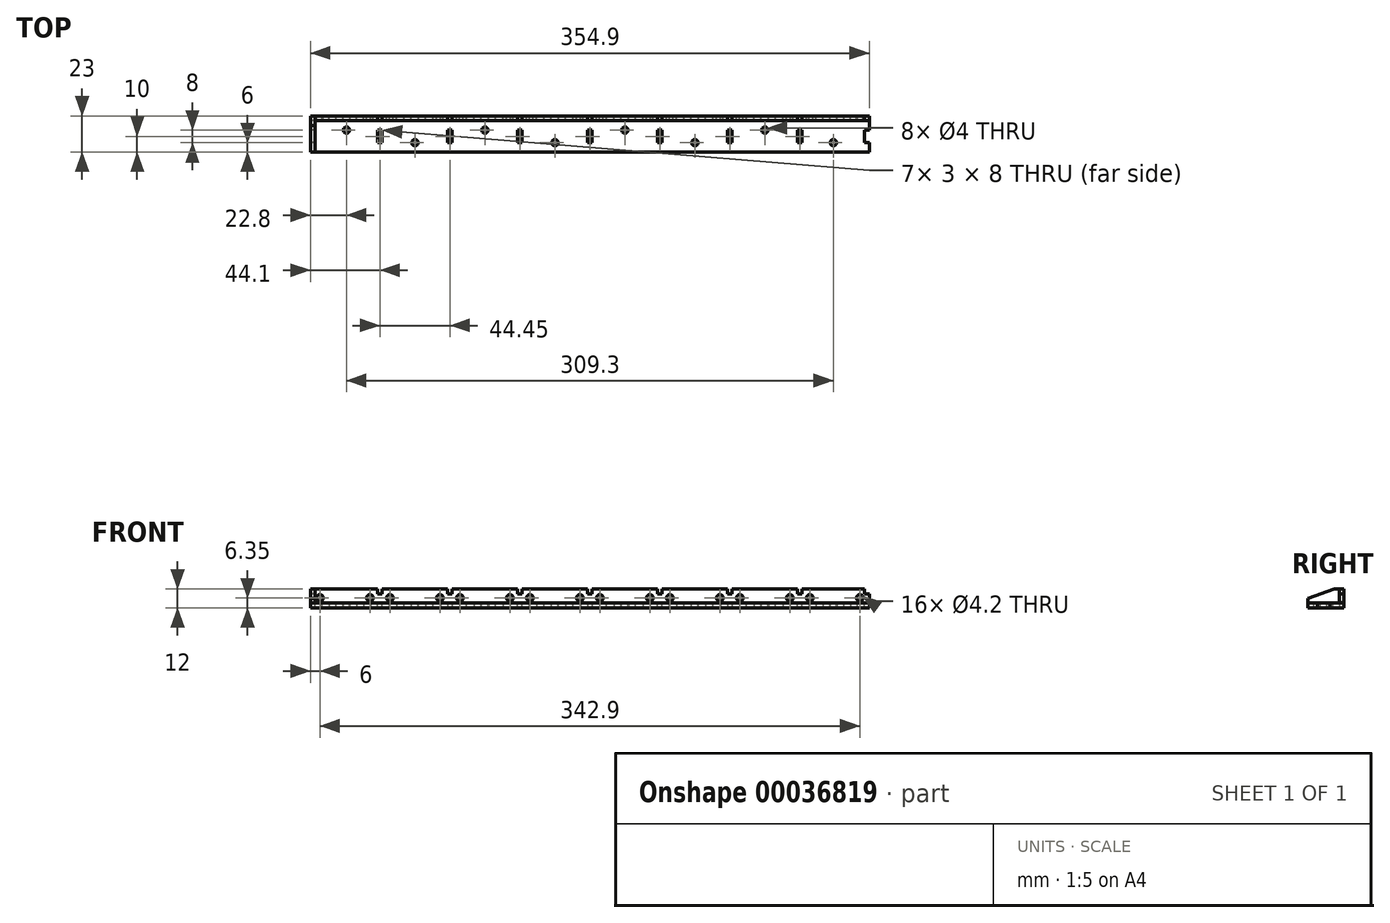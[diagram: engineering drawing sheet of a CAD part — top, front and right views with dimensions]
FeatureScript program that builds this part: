
annotation { "Feature Type Name" : "Feature", "Feature Type Description" : "" }
export const myFeature = defineFeature(function(context is Context, id is Id, definition is map)
    precondition{}
    {
        {
            var Q0;
            Q0=qCreatedBy(makeId("Front.planeOp"),FACE);
            var sketch = newSketch(context, id + "F0", { "sketchPlane" : qUnion([Q0])});
            skLineSegment(sketch, "E0.bottom", {"start": v(0, 0) * mm, "end": v(354.9, 0) * mm});
            skLineSegment(sketch, "E0.top", {"start": v(0, 12) * mm, "end": v(354.9, 12) * mm});
            skLineSegment(sketch, "E0.left", {"start": v(0, 0) * mm, "end": v(0, 12) * mm});
            skLineSegment(sketch, "E0.right", {"start": v(354.9, 0) * mm, "end": v(354.9, 12) * mm});
            skCircle(sketch, "E1", {"center": v(6, 6.35) * mm, "radius": 2.1 * mm});
            skCircle(sketch, "E2", {"center": v(37.75, 6.35) * mm, "radius": 2.1 * mm});
            skCircle(sketch, "E3", {"center": v(50.45, 6.35) * mm, "radius": 2.1 * mm});
            skCircle(sketch, "E4", {"center": v(82.2, 6.35) * mm, "radius": 2.1 * mm});
            skCircle(sketch, "E5", {"center": v(94.9, 6.35) * mm, "radius": 2.1 * mm});
            skCircle(sketch, "E6", {"center": v(126.65, 6.35) * mm, "radius": 2.1 * mm});
            skCircle(sketch, "E7", {"center": v(139.35, 6.35) * mm, "radius": 2.1 * mm});
            skCircle(sketch, "E8", {"center": v(171.1, 6.35) * mm, "radius": 2.1 * mm});
            skCircle(sketch, "E9", {"center": v(183.8, 6.35) * mm, "radius": 2.1 * mm});
            skCircle(sketch, "E10", {"center": v(215.55, 6.35) * mm, "radius": 2.1 * mm});
            skCircle(sketch, "E11", {"center": v(228.25, 6.35) * mm, "radius": 2.1 * mm});
            skCircle(sketch, "E12", {"center": v(260, 6.35) * mm, "radius": 2.1 * mm});
            skCircle(sketch, "E13", {"center": v(272.7, 6.35) * mm, "radius": 2.1 * mm});
            skCircle(sketch, "E14", {"center": v(304.45, 6.35) * mm, "radius": 2.1 * mm});
            skCircle(sketch, "E15", {"center": v(317.15, 6.35) * mm, "radius": 2.1 * mm});
            skCircle(sketch, "E16", {"center": v(348.9, 6.35) * mm, "radius": 2.1 * mm});
            skLineSegment(sketch, "E17", {"start": v(6, 6.35) * mm, "end": v(37.75, 6.35) * mm, "construction": true});
            skLineSegment(sketch, "E18", {"start": v(50.45, 6.35) * mm, "end": v(82.2, 6.35) * mm, "construction": true});
            skLineSegment(sketch, "E19", {"start": v(94.9, 6.35) * mm, "end": v(126.65, 6.35) * mm, "construction": true});
            skLineSegment(sketch, "E20", {"start": v(139.35, 6.35) * mm, "end": v(171.1, 6.35) * mm, "construction": true});
            skLineSegment(sketch, "E21", {"start": v(183.8, 6.35) * mm, "end": v(215.55, 6.35) * mm, "construction": true});
            skLineSegment(sketch, "E22", {"start": v(228.25, 6.35) * mm, "end": v(260, 6.35) * mm, "construction": true});
            skLineSegment(sketch, "E23", {"start": v(272.7, 6.35) * mm, "end": v(304.45, 6.35) * mm, "construction": true});
            skLineSegment(sketch, "E24", {"start": v(317.15, 6.35) * mm, "end": v(348.9, 6.35) * mm, "construction": true});
            skLineSegment(sketch, "E25", {"start": v(37.75, 6.35) * mm, "end": v(50.45, 6.35) * mm, "construction": true});
            skLineSegment(sketch, "E26", {"start": v(82.2, 6.35) * mm, "end": v(94.9, 6.35) * mm, "construction": true});
            skLineSegment(sketch, "E27", {"start": v(126.65, 6.35) * mm, "end": v(139.35, 6.35) * mm, "construction": true});
            skLineSegment(sketch, "E28", {"start": v(171.1, 6.35) * mm, "end": v(183.8, 6.35) * mm, "construction": true});
            skLineSegment(sketch, "E29", {"start": v(215.55, 6.35) * mm, "end": v(228.25, 6.35) * mm, "construction": true});
            skLineSegment(sketch, "E30", {"start": v(260, 6.35) * mm, "end": v(272.7, 6.35) * mm, "construction": true});
            skLineSegment(sketch, "E31", {"start": v(304.45, 6.35) * mm, "end": v(317.15, 6.35) * mm, "construction": true});
            skLineSegment(sketch, "E32", {"start": v(6, 6.35) * mm, "end": v(0, 6.35) * mm, "construction": true});
            skLineSegment(sketch, "E33", {"start": v(348.9, 6.35) * mm, "end": v(354.9, 6.35) * mm, "construction": true});
            skPoint(sketch, "E34", {"position": v(44.1, 6.35) * mm});
            skPoint(sketch, "E35", {"position": v(88.55, 6.35) * mm});
            skPoint(sketch, "E36", {"position": v(133, 6.35) * mm});
            skPoint(sketch, "E37", {"position": v(177.45, 6.35) * mm});
            skPoint(sketch, "E38", {"position": v(221.9, 6.35) * mm});
            skPoint(sketch, "E39", {"position": v(266.35, 6.35) * mm});
            skPoint(sketch, "E40", {"position": v(310.8, 6.35) * mm});
            skCircle(sketch, "E41", {"center": v(50.45, 6.35) * mm, "radius": 2.5 * mm, "construction": true});
            skSolve(sketch);
        }
        {
            var Q0;
            Q0=makeQuery(id+"F0.imprint","IMPRINT",FACE,{"disambiguationData":[TD([[makeQuery(id+"F0.imprint","IMPRINT",EDGE,{"derivedFrom":sQuery(id+"F0.wireOp",EDGE,"E0.bottom")}),1.0]])]});
            var sketch = newSketch(context, id + "F1", { "sketchPlane" : qUnion([Q0])});
            skLineSegment(sketch, "E42", {"start": v(44.1, 6.35) * mm, "end": v(44.1, 0) * mm, "construction": true});
            skLineSegment(sketch, "E43", {"start": v(88.55, 6.35) * mm, "end": v(88.55, 0) * mm, "construction": true});
            skLineSegment(sketch, "E44", {"start": v(133, 6.35) * mm, "end": v(133, 0) * mm, "construction": true});
            skLineSegment(sketch, "E45.MirrorCS", {"start": v(177.45, 6.35) * mm, "end": v(177.45, 0) * mm});
            skLineSegment(sketch, "E46.MirrorCS", {"start": v(221.9, 6.35) * mm, "end": v(221.9, 0) * mm});
            skLineSegment(sketch, "E47", {"start": v(266.35, 6.35) * mm, "end": v(266.35, 0) * mm, "construction": true});
            skLineSegment(sketch, "E48.MirrorCS", {"start": v(310.8, 6.35) * mm, "end": v(310.8, 0) * mm});
            skLineSegment(sketch, "E49.bottom", {"start": v(0, 0) * mm, "end": v(3, 0) * mm});
            skLineSegment(sketch, "E49.top", {"start": v(0, 3) * mm, "end": v(3, 3) * mm});
            skLineSegment(sketch, "E49.left", {"start": v(0, 0) * mm, "end": v(0, 3) * mm});
            skLineSegment(sketch, "E49.right", {"start": v(3, 0) * mm, "end": v(3, 3) * mm});
            skLineSegment(sketch, "E50.bottom", {"start": v(42.6, 0) * mm, "end": v(45.6, 0) * mm});
            skLineSegment(sketch, "E50.top", {"start": v(42.6, 3) * mm, "end": v(45.6, 3) * mm});
            skLineSegment(sketch, "E50.left", {"start": v(42.6, 0) * mm, "end": v(42.6, 3) * mm});
            skLineSegment(sketch, "E50.right", {"start": v(45.6, 0) * mm, "end": v(45.6, 3) * mm});
            skPoint(sketch, "E51", {"position": v(44.1, 0) * mm});
            skLineSegment(sketch, "E52.MirrorCS", {"start": v(354.9, 3) * mm, "end": v(351.9, 3) * mm});
            skLineSegment(sketch, "E53.MirrorCS", {"start": v(351.9, 0) * mm, "end": v(351.9, 3) * mm});
            skLineSegment(sketch, "E54.MirrorCS", {"start": v(354.9, 0) * mm, "end": v(351.9, 0) * mm, "construction": true});
            skLineSegment(sketch, "E55.MirrorCS", {"start": v(354.9, 0) * mm, "end": v(354.9, 3) * mm, "construction": true});
            skLineSegment(sketch, "E56", {"start": v(351.9, 0) * mm, "end": v(354.9, 0) * mm});
            skLineSegment(sketch, "E57", {"start": v(354.9, 3) * mm, "end": v(354.9, 0) * mm});
            skLineSegment(sketch, "E58.MirrorCS", {"start": v(131.5, 0) * mm, "end": v(131.5, 3) * mm});
            skLineSegment(sketch, "E59.MirrorCS", {"start": v(134.5, 0) * mm, "end": v(134.5, 3) * mm});
            skPoint(sketch, "E60.MirrorP", {"position": v(133, 0) * mm});
            skLineSegment(sketch, "E61.MirrorCS", {"start": v(134.5, 3) * mm, "end": v(131.5, 3) * mm});
            skLineSegment(sketch, "E62.MirrorCS", {"start": v(134.5, 0) * mm, "end": v(131.5, 0) * mm});
            skLineSegment(sketch, "E63.MirrorCS", {"start": v(312.3, 0) * mm, "end": v(309.3, 0) * mm});
            skLineSegment(sketch, "E64.MirrorCS", {"start": v(312.3, 0) * mm, "end": v(312.3, 3) * mm});
            skLineSegment(sketch, "E65.MirrorCS", {"start": v(309.3, 0) * mm, "end": v(309.3, 3) * mm});
            skLineSegment(sketch, "E66.MirrorCS", {"start": v(312.3, 3) * mm, "end": v(309.3, 3) * mm});
            skPoint(sketch, "E67.MirrorP", {"position": v(310.8, 0) * mm});
            skLineSegment(sketch, "E68.MirrorCS", {"start": v(220.4, 0) * mm, "end": v(223.4, 0) * mm});
            skLineSegment(sketch, "E69.MirrorCS", {"start": v(223.4, 0) * mm, "end": v(223.4, 3) * mm});
            skLineSegment(sketch, "E70.MirrorCS", {"start": v(220.4, 0) * mm, "end": v(220.4, 3) * mm});
            skLineSegment(sketch, "E71.MirrorCS", {"start": v(220.4, 3) * mm, "end": v(223.4, 3) * mm});
            skLineSegment(sketch, "E72.bottom", {"start": v(87.05, 3) * mm, "end": v(90.05, 3) * mm});
            skLineSegment(sketch, "E72.top", {"start": v(87.05, 0) * mm, "end": v(90.05, 0) * mm});
            skLineSegment(sketch, "E72.left", {"start": v(87.05, 3) * mm, "end": v(87.05, 0) * mm});
            skLineSegment(sketch, "E72.right", {"start": v(90.05, 3) * mm, "end": v(90.05, 0) * mm});
            skLineSegment(sketch, "E73.MirrorCS", {"start": v(178.95, 3) * mm, "end": v(175.95, 3) * mm});
            skLineSegment(sketch, "E74.MirrorCS", {"start": v(178.95, 3) * mm, "end": v(178.95, 0) * mm});
            skLineSegment(sketch, "E75.MirrorCS", {"start": v(178.95, 0) * mm, "end": v(175.95, 0) * mm});
            skLineSegment(sketch, "E76.MirrorCS", {"start": v(175.95, 3) * mm, "end": v(175.95, 0) * mm});
            skLineSegment(sketch, "E77.MirrorCS", {"start": v(264.85, 3) * mm, "end": v(267.85, 3) * mm});
            skLineSegment(sketch, "E78.MirrorCS", {"start": v(264.85, 0) * mm, "end": v(267.85, 0) * mm});
            skLineSegment(sketch, "E79.MirrorCS", {"start": v(267.85, 3) * mm, "end": v(267.85, 0) * mm});
            skLineSegment(sketch, "E80.MirrorCS", {"start": v(264.85, 3) * mm, "end": v(264.85, 0) * mm});
            skLineSegment(sketch, "E81", {"start": v(42.6, 3) * mm, "end": v(38.2, 3) * mm, "construction": true});
            skLineSegment(sketch, "E82", {"start": v(38.2, 3) * mm, "end": v(33.8, 3) * mm});
            skLineSegment(sketch, "E83", {"start": v(33.8, 3) * mm, "end": v(29.4, 3) * mm, "construction": true});
            skLineSegment(sketch, "E84", {"start": v(29.4, 3) * mm, "end": v(25, 3) * mm});
            skLineSegment(sketch, "E85", {"start": v(25, 3) * mm, "end": v(20.6, 3) * mm, "construction": true});
            skLineSegment(sketch, "E86", {"start": v(20.6, 3) * mm, "end": v(16.2, 3) * mm});
            skLineSegment(sketch, "E87", {"start": v(16.2, 3) * mm, "end": v(11.8, 3) * mm, "construction": true});
            skLineSegment(sketch, "E88", {"start": v(11.8, 3) * mm, "end": v(7.4, 3) * mm});
            skLineSegment(sketch, "E89", {"start": v(7.4, 3) * mm, "end": v(3, 3) * mm, "construction": true});
            skLineSegment(sketch, "E90", {"start": v(38.2, 3) * mm, "end": v(38.2, 0) * mm});
            skLineSegment(sketch, "E91", {"start": v(33.8, 3) * mm, "end": v(33.8, 0) * mm});
            skLineSegment(sketch, "E92", {"start": v(33.8, 0) * mm, "end": v(38.2, 0) * mm});
            skLineSegment(sketch, "E93", {"start": v(29.4, 3) * mm, "end": v(29.4, 0) * mm});
            skLineSegment(sketch, "E94", {"start": v(29.4, 0) * mm, "end": v(25, 0) * mm});
            skLineSegment(sketch, "E95", {"start": v(25, 0) * mm, "end": v(25, 3) * mm});
            skLineSegment(sketch, "E96", {"start": v(20.6, 3) * mm, "end": v(20.6, 0) * mm});
            skLineSegment(sketch, "E97", {"start": v(20.6, 0) * mm, "end": v(16.2, 0) * mm});
            skLineSegment(sketch, "E98", {"start": v(16.2, 0) * mm, "end": v(16.2, 3) * mm});
            skLineSegment(sketch, "E99", {"start": v(11.8, 3) * mm, "end": v(11.8, 0) * mm});
            skLineSegment(sketch, "E100", {"start": v(11.8, 0) * mm, "end": v(7.4, 0) * mm});
            skLineSegment(sketch, "E101", {"start": v(7.4, 0) * mm, "end": v(7.4, 3) * mm});
            skLineSegment(sketch, "E102.MirrorCS", {"start": v(325.5, 3) * mm, "end": v(329.9, 3) * mm});
            skLineSegment(sketch, "E103.MirrorCS", {"start": v(329.9, 0) * mm, "end": v(329.9, 3) * mm});
            skLineSegment(sketch, "E104.MirrorCS", {"start": v(325.5, 0) * mm, "end": v(329.9, 0) * mm});
            skLineSegment(sketch, "E105.MirrorCS", {"start": v(321.1, 3) * mm, "end": v(325.5, 3) * mm, "construction": true});
            skLineSegment(sketch, "E106.MirrorCS", {"start": v(338.7, 3) * mm, "end": v(343.1, 3) * mm, "construction": true});
            skLineSegment(sketch, "E107.MirrorCS", {"start": v(329.9, 3) * mm, "end": v(334.3, 3) * mm, "construction": true});
            skLineSegment(sketch, "E108.MirrorCS", {"start": v(334.3, 0) * mm, "end": v(338.7, 0) * mm});
            skLineSegment(sketch, "E109.MirrorCS", {"start": v(334.3, 3) * mm, "end": v(338.7, 3) * mm});
            skLineSegment(sketch, "E110.MirrorCS", {"start": v(316.7, 3) * mm, "end": v(316.7, 0) * mm});
            skLineSegment(sketch, "E111.MirrorCS", {"start": v(316.7, 3) * mm, "end": v(321.1, 3) * mm});
            skLineSegment(sketch, "E112.MirrorCS", {"start": v(334.3, 3) * mm, "end": v(334.3, 0) * mm});
            skLineSegment(sketch, "E113.MirrorCS", {"start": v(321.1, 3) * mm, "end": v(321.1, 0) * mm});
            skLineSegment(sketch, "E114.MirrorCS", {"start": v(338.7, 0) * mm, "end": v(338.7, 3) * mm});
            skLineSegment(sketch, "E115.MirrorCS", {"start": v(325.5, 3) * mm, "end": v(325.5, 0) * mm});
            skLineSegment(sketch, "E116.MirrorCS", {"start": v(343.1, 3) * mm, "end": v(343.1, 0) * mm});
            skLineSegment(sketch, "E117.MirrorCS", {"start": v(347.5, 0) * mm, "end": v(347.5, 3) * mm});
            skLineSegment(sketch, "E118.MirrorCS", {"start": v(343.1, 0) * mm, "end": v(347.5, 0) * mm});
            skLineSegment(sketch, "E119.MirrorCS", {"start": v(321.1, 0) * mm, "end": v(316.7, 0) * mm});
            skLineSegment(sketch, "E120.MirrorCS", {"start": v(343.1, 3) * mm, "end": v(347.5, 3) * mm});
            skLineSegment(sketch, "E121", {"start": v(59.42, 3) * mm, "end": v(64.02, 3) * mm});
            skLineSegment(sketch, "E122", {"start": v(64.02, 3) * mm, "end": v(68.63, 3) * mm, "construction": true});
            skLineSegment(sketch, "E123", {"start": v(68.63, 3) * mm, "end": v(73.23, 3) * mm});
            skLineSegment(sketch, "E124", {"start": v(73.23, 3) * mm, "end": v(77.84, 3) * mm, "construction": true});
            skLineSegment(sketch, "E125", {"start": v(77.84, 3) * mm, "end": v(82.44, 3) * mm});
            skLineSegment(sketch, "E126", {"start": v(82.44, 3) * mm, "end": v(87.05, 3) * mm, "construction": true});
            skLineSegment(sketch, "E127", {"start": v(82.44, 3) * mm, "end": v(82.44, 0) * mm});
            skLineSegment(sketch, "E128", {"start": v(82.44, 0) * mm, "end": v(77.84, 0) * mm});
            skLineSegment(sketch, "E129", {"start": v(77.84, 0) * mm, "end": v(77.84, 3) * mm});
            skLineSegment(sketch, "E130", {"start": v(73.23, 3) * mm, "end": v(73.23, 0) * mm});
            skLineSegment(sketch, "E131", {"start": v(73.23, 0) * mm, "end": v(68.63, 0) * mm});
            skLineSegment(sketch, "E132", {"start": v(68.63, 0) * mm, "end": v(68.63, 3) * mm});
            skLineSegment(sketch, "E133", {"start": v(64.02, 3) * mm, "end": v(64.02, 0) * mm});
            skLineSegment(sketch, "E134", {"start": v(64.02, 0) * mm, "end": v(59.42, 0) * mm});
            skLineSegment(sketch, "E135", {"start": v(59.42, 0) * mm, "end": v(59.42, 3) * mm});
            skLineSegment(sketch, "E136", {"start": v(59.42, 3) * mm, "end": v(54.81, 3) * mm, "construction": true});
            skLineSegment(sketch, "E137", {"start": v(54.81, 3) * mm, "end": v(54.81, 0) * mm});
            skLineSegment(sketch, "E138", {"start": v(54.81, 0) * mm, "end": v(50.2, 0) * mm});
            skLineSegment(sketch, "E139", {"start": v(50.2, 0) * mm, "end": v(50.2, 3) * mm});
            skLineSegment(sketch, "E140", {"start": v(50.2, 3) * mm, "end": v(54.81, 3) * mm});
            skLineSegment(sketch, "E141", {"start": v(50.2, 3) * mm, "end": v(45.6, 3) * mm, "construction": true});
            skLineSegment(sketch, "E142.MirrorCS", {"start": v(113.08, 3) * mm, "end": v(113.08, 0) * mm});
            skLineSegment(sketch, "E143.MirrorCS", {"start": v(122.29, 3) * mm, "end": v(122.29, 0) * mm});
            skLineSegment(sketch, "E144.MirrorCS", {"start": v(126.9, 0) * mm, "end": v(126.9, 3) * mm});
            skLineSegment(sketch, "E145.MirrorCS", {"start": v(94.66, 3) * mm, "end": v(94.66, 0) * mm});
            skLineSegment(sketch, "E146.MirrorCS", {"start": v(117.68, 3) * mm, "end": v(122.29, 3) * mm, "construction": true});
            skLineSegment(sketch, "E147.MirrorCS", {"start": v(113.08, 0) * mm, "end": v(117.68, 0) * mm});
            skLineSegment(sketch, "E148.MirrorCS", {"start": v(113.08, 3) * mm, "end": v(108.47, 3) * mm, "construction": true});
            skLineSegment(sketch, "E149.MirrorCS", {"start": v(103.87, 3) * mm, "end": v(99.26, 3) * mm, "construction": true});
            skLineSegment(sketch, "E150.MirrorCS", {"start": v(103.87, 0) * mm, "end": v(108.47, 0) * mm});
            skLineSegment(sketch, "E151.MirrorCS", {"start": v(117.68, 3) * mm, "end": v(113.08, 3) * mm});
            skLineSegment(sketch, "E152.MirrorCS", {"start": v(117.68, 0) * mm, "end": v(117.68, 3) * mm});
            skLineSegment(sketch, "E153.MirrorCS", {"start": v(108.47, 3) * mm, "end": v(103.87, 3) * mm});
            skLineSegment(sketch, "E154.MirrorCS", {"start": v(99.26, 3) * mm, "end": v(94.66, 3) * mm});
            skLineSegment(sketch, "E155.MirrorCS", {"start": v(103.87, 3) * mm, "end": v(103.87, 0) * mm});
            skLineSegment(sketch, "E156.MirrorCS", {"start": v(108.47, 0) * mm, "end": v(108.47, 3) * mm});
            skLineSegment(sketch, "E157.MirrorCS", {"start": v(99.26, 0) * mm, "end": v(99.26, 3) * mm});
            skLineSegment(sketch, "E158.MirrorCS", {"start": v(122.29, 0) * mm, "end": v(126.9, 0) * mm});
            skLineSegment(sketch, "E159.MirrorCS", {"start": v(94.66, 0) * mm, "end": v(99.26, 0) * mm});
            skLineSegment(sketch, "E160.MirrorCS", {"start": v(126.9, 3) * mm, "end": v(122.29, 3) * mm});
            skLineSegment(sketch, "E161.MirrorCS", {"start": v(148.32, 3) * mm, "end": v(143.71, 3) * mm, "construction": true});
            skLineSegment(sketch, "E162.MirrorCS", {"start": v(148.32, 3) * mm, "end": v(152.92, 3) * mm});
            skLineSegment(sketch, "E163.MirrorCS", {"start": v(157.53, 3) * mm, "end": v(162.13, 3) * mm});
            skLineSegment(sketch, "E164.MirrorCS", {"start": v(162.13, 3) * mm, "end": v(166.74, 3) * mm, "construction": true});
            skLineSegment(sketch, "E165.MirrorCS", {"start": v(152.92, 3) * mm, "end": v(157.53, 3) * mm, "construction": true});
            skLineSegment(sketch, "E166.MirrorCS", {"start": v(143.71, 3) * mm, "end": v(143.71, 0) * mm});
            skLineSegment(sketch, "E167.MirrorCS", {"start": v(162.13, 3) * mm, "end": v(162.13, 0) * mm});
            skLineSegment(sketch, "E168.MirrorCS", {"start": v(171.34, 0) * mm, "end": v(166.74, 0) * mm});
            skLineSegment(sketch, "E169.MirrorCS", {"start": v(139.1, 0) * mm, "end": v(139.1, 3) * mm});
            skLineSegment(sketch, "E170.MirrorCS", {"start": v(171.34, 3) * mm, "end": v(171.34, 0) * mm});
            skLineSegment(sketch, "E171.MirrorCS", {"start": v(148.32, 0) * mm, "end": v(148.32, 3) * mm});
            skLineSegment(sketch, "E172.MirrorCS", {"start": v(157.53, 0) * mm, "end": v(157.53, 3) * mm});
            skLineSegment(sketch, "E173.MirrorCS", {"start": v(166.74, 3) * mm, "end": v(171.34, 3) * mm});
            skLineSegment(sketch, "E174.MirrorCS", {"start": v(152.92, 0) * mm, "end": v(148.32, 0) * mm});
            skLineSegment(sketch, "E175.MirrorCS", {"start": v(152.92, 3) * mm, "end": v(152.92, 0) * mm});
            skLineSegment(sketch, "E176.MirrorCS", {"start": v(162.13, 0) * mm, "end": v(157.53, 0) * mm});
            skLineSegment(sketch, "E177.MirrorCS", {"start": v(166.74, 0) * mm, "end": v(166.74, 3) * mm});
            skLineSegment(sketch, "E178.MirrorCS", {"start": v(143.71, 0) * mm, "end": v(139.1, 0) * mm});
            skLineSegment(sketch, "E179.MirrorCS", {"start": v(139.1, 3) * mm, "end": v(143.71, 3) * mm});
            skLineSegment(sketch, "E180.MirrorCS", {"start": v(206.58, 3) * mm, "end": v(211.19, 3) * mm, "construction": true});
            skLineSegment(sketch, "E181.MirrorCS", {"start": v(192.77, 3) * mm, "end": v(188.16, 3) * mm, "construction": true});
            skLineSegment(sketch, "E182.MirrorCS", {"start": v(201.98, 3) * mm, "end": v(197.37, 3) * mm, "construction": true});
            skLineSegment(sketch, "E183.MirrorCS", {"start": v(197.37, 3) * mm, "end": v(192.77, 3) * mm});
            skLineSegment(sketch, "E184.MirrorCS", {"start": v(206.58, 3) * mm, "end": v(201.98, 3) * mm});
            skLineSegment(sketch, "E185.MirrorCS", {"start": v(183.56, 3) * mm, "end": v(183.56, 0) * mm});
            skLineSegment(sketch, "E186.MirrorCS", {"start": v(211.19, 3) * mm, "end": v(211.19, 0) * mm});
            skLineSegment(sketch, "E187.MirrorCS", {"start": v(197.37, 0) * mm, "end": v(197.37, 3) * mm});
            skLineSegment(sketch, "E188.MirrorCS", {"start": v(201.98, 3) * mm, "end": v(201.98, 0) * mm});
            skLineSegment(sketch, "E189.MirrorCS", {"start": v(188.16, 3) * mm, "end": v(183.56, 3) * mm});
            skLineSegment(sketch, "E190.MirrorCS", {"start": v(215.8, 0) * mm, "end": v(215.8, 3) * mm});
            skLineSegment(sketch, "E191.MirrorCS", {"start": v(192.77, 3) * mm, "end": v(192.77, 0) * mm});
            skLineSegment(sketch, "E192.MirrorCS", {"start": v(192.77, 0) * mm, "end": v(197.37, 0) * mm});
            skLineSegment(sketch, "E193.MirrorCS", {"start": v(183.56, 0) * mm, "end": v(188.16, 0) * mm});
            skLineSegment(sketch, "E194.MirrorCS", {"start": v(206.58, 0) * mm, "end": v(206.58, 3) * mm});
            skLineSegment(sketch, "E195.MirrorCS", {"start": v(188.16, 0) * mm, "end": v(188.16, 3) * mm});
            skLineSegment(sketch, "E196.MirrorCS", {"start": v(201.98, 0) * mm, "end": v(206.58, 0) * mm});
            skLineSegment(sketch, "E197.MirrorCS", {"start": v(215.8, 3) * mm, "end": v(211.19, 3) * mm});
            skLineSegment(sketch, "E198.MirrorCS", {"start": v(211.19, 0) * mm, "end": v(215.8, 0) * mm});
            skLineSegment(sketch, "E199.MirrorCS", {"start": v(251.03, 3) * mm, "end": v(255.64, 3) * mm, "construction": true});
            skLineSegment(sketch, "E200.MirrorCS", {"start": v(241.82, 3) * mm, "end": v(246.43, 3) * mm, "construction": true});
            skLineSegment(sketch, "E201.MirrorCS", {"start": v(237.22, 3) * mm, "end": v(232.61, 3) * mm, "construction": true});
            skLineSegment(sketch, "E202.MirrorCS", {"start": v(237.22, 3) * mm, "end": v(241.82, 3) * mm});
            skLineSegment(sketch, "E203.MirrorCS", {"start": v(260.24, 0) * mm, "end": v(255.64, 0) * mm});
            skLineSegment(sketch, "E204.MirrorCS", {"start": v(241.82, 0) * mm, "end": v(237.22, 0) * mm});
            skLineSegment(sketch, "E205.MirrorCS", {"start": v(228, 0) * mm, "end": v(228, 3) * mm});
            skLineSegment(sketch, "E206.MirrorCS", {"start": v(241.82, 3) * mm, "end": v(241.82, 0) * mm});
            skLineSegment(sketch, "E207.MirrorCS", {"start": v(260.24, 3) * mm, "end": v(260.24, 0) * mm});
            skLineSegment(sketch, "E208.MirrorCS", {"start": v(232.61, 0) * mm, "end": v(228, 0) * mm});
            skLineSegment(sketch, "E209.MirrorCS", {"start": v(251.03, 3) * mm, "end": v(251.03, 0) * mm});
            skLineSegment(sketch, "E210.MirrorCS", {"start": v(246.43, 0) * mm, "end": v(246.43, 3) * mm});
            skLineSegment(sketch, "E211.MirrorCS", {"start": v(228, 3) * mm, "end": v(232.61, 3) * mm});
            skLineSegment(sketch, "E212.MirrorCS", {"start": v(232.61, 3) * mm, "end": v(232.61, 0) * mm});
            skLineSegment(sketch, "E213.MirrorCS", {"start": v(255.64, 3) * mm, "end": v(260.24, 3) * mm});
            skLineSegment(sketch, "E214.MirrorCS", {"start": v(255.64, 0) * mm, "end": v(255.64, 3) * mm});
            skLineSegment(sketch, "E215.MirrorCS", {"start": v(237.22, 0) * mm, "end": v(237.22, 3) * mm});
            skLineSegment(sketch, "E216.MirrorCS", {"start": v(246.43, 3) * mm, "end": v(251.03, 3) * mm});
            skLineSegment(sketch, "E217.MirrorCS", {"start": v(251.03, 0) * mm, "end": v(246.43, 0) * mm});
            skLineSegment(sketch, "E218.MirrorCS", {"start": v(295.48, 3) * mm, "end": v(290.88, 3) * mm});
            skLineSegment(sketch, "E219.MirrorCS", {"start": v(286.27, 3) * mm, "end": v(281.67, 3) * mm});
            skLineSegment(sketch, "E220.MirrorCS", {"start": v(295.48, 3) * mm, "end": v(300.09, 3) * mm, "construction": true});
            skLineSegment(sketch, "E221.MirrorCS", {"start": v(290.88, 3) * mm, "end": v(286.27, 3) * mm, "construction": true});
            skLineSegment(sketch, "E222.MirrorCS", {"start": v(281.67, 3) * mm, "end": v(277.06, 3) * mm, "construction": true});
            skLineSegment(sketch, "E223.MirrorCS", {"start": v(272.46, 3) * mm, "end": v(272.46, 0) * mm});
            skLineSegment(sketch, "E224.MirrorCS", {"start": v(281.67, 3) * mm, "end": v(281.67, 0) * mm});
            skLineSegment(sketch, "E225.MirrorCS", {"start": v(286.27, 0) * mm, "end": v(286.27, 3) * mm});
            skLineSegment(sketch, "E226.MirrorCS", {"start": v(304.7, 3) * mm, "end": v(300.09, 3) * mm});
            skLineSegment(sketch, "E227.MirrorCS", {"start": v(290.88, 3) * mm, "end": v(290.88, 0) * mm});
            skLineSegment(sketch, "E228.MirrorCS", {"start": v(295.48, 0) * mm, "end": v(295.48, 3) * mm});
            skLineSegment(sketch, "E229.MirrorCS", {"start": v(304.7, 0) * mm, "end": v(304.7, 3) * mm});
            skLineSegment(sketch, "E230.MirrorCS", {"start": v(290.88, 0) * mm, "end": v(295.48, 0) * mm});
            skLineSegment(sketch, "E231.MirrorCS", {"start": v(272.46, 0) * mm, "end": v(277.06, 0) * mm});
            skLineSegment(sketch, "E232.MirrorCS", {"start": v(277.06, 3) * mm, "end": v(272.46, 3) * mm});
            skLineSegment(sketch, "E233.MirrorCS", {"start": v(300.09, 0) * mm, "end": v(304.7, 0) * mm});
            skLineSegment(sketch, "E234.MirrorCS", {"start": v(300.09, 3) * mm, "end": v(300.09, 0) * mm});
            skLineSegment(sketch, "E235.MirrorCS", {"start": v(281.67, 0) * mm, "end": v(286.27, 0) * mm});
            skLineSegment(sketch, "E236.MirrorCS", {"start": v(277.06, 0) * mm, "end": v(277.06, 3) * mm});
            skSolve(sketch);
        }
        {
            var Q0;
            Q0=qCreatedBy(makeId("Front.planeOp"),FACE);
            var sketch = newSketch(context, id + "F2", { "sketchPlane" : qUnion([Q0])});
            skLineSegment(sketch, "E237.bottom", {"start": v(0, 0) * mm, "end": v(354.9, 0) * mm});
            skLineSegment(sketch, "E237.top", {"start": v(0, 3) * mm, "end": v(354.9, 3) * mm});
            skLineSegment(sketch, "E237.left", {"start": v(0, 0) * mm, "end": v(0, 3) * mm});
            skLineSegment(sketch, "E237.right", {"start": v(354.9, 0) * mm, "end": v(354.9, 3) * mm});
            skSolve(sketch);
        }
        {
            var Q0;
            Q0 = qSketchRegion(id + "F0", true);
            extrude(context, id + "F3", {"entities" : qUnion([Q0]), "offsetDistance" : 25 * mm, "depth" : 3 * mm});
        }
        {
            var Q0;
            Q0=makeQuery(id+"F1.imprint","IMPRINT",FACE,{"disambiguationData":[TD([[makeQuery(id+"F1.imprint","IMPRINT",EDGE,{"derivedFrom":sQuery(id+"F1.wireOp",EDGE,"E49.bottom")}),1.0]])]});
            var Q1;
            Q1=makeQuery(id+"F1.imprint","IMPRINT",FACE,{"disambiguationData":[TD([[makeQuery(id+"F1.imprint","IMPRINT",EDGE,{"derivedFrom":sQuery(id+"F1.wireOp",EDGE,"6a9f6b4e-8c17-479e-95aa-c868ed02bcc8.bottom")}),1.0]])]});
            var Q2;
            Q2=makeQuery(id+"F1.imprint","IMPRINT",FACE,{"disambiguationData":[TD([[makeQuery(id+"F1.imprint","IMPRINT",EDGE,{"derivedFrom":sQuery(id+"F1.wireOp",EDGE,"d0e4a734-2a00-432a-b971-5d8aa04fd6d9.bottom")}),1.0]])]});
            var Q3;
            Q3=makeQuery(id+"F1.imprint","IMPRINT",FACE,{"disambiguationData":[TD([[makeQuery(id+"F1.imprint","IMPRINT",EDGE,{"derivedFrom":sQuery(id+"F1.wireOp",EDGE,"0fa12c67-d307-4137-8aa7-c6dfb889ed58.bottom")}),1.0]])]});
            var Q4;
            Q4=makeQuery(id+"F1.imprint","IMPRINT",FACE,{"disambiguationData":[TD([[makeQuery(id+"F1.imprint","IMPRINT",EDGE,{"derivedFrom":sQuery(id+"F1.wireOp",EDGE,"b24369ca-d6b9-488d-87b8-04e79b56e681.bottom")}),1.0]])]});
            var Q5;
            Q5=makeQuery(id+"F1.imprint","IMPRINT",FACE,{"disambiguationData":[TD([[makeQuery(id+"F1.imprint","IMPRINT",EDGE,{"derivedFrom":sQuery(id+"F1.wireOp",EDGE,"bdd40437-d99c-4cb8-ad16-0bfbec51b95a.bottom")}),1.0]])]});
            var Q6;
            Q6=makeQuery(id+"F1.imprint","IMPRINT",FACE,{"disambiguationData":[TD([[makeQuery(id+"F1.imprint","IMPRINT",EDGE,{"derivedFrom":sQuery(id+"F1.wireOp",EDGE,"855304bd-eab8-4061-b494-b8053609a213.bottom")}),1.0]])]});
            var Q7;
            Q7=makeQuery(id+"F1.imprint","IMPRINT",FACE,{"disambiguationData":[TD([[makeQuery(id+"F1.imprint","IMPRINT",EDGE,{"derivedFrom":sQuery(id+"F1.wireOp",EDGE,"E50.bottom")}),1.0]])]});
            var Q8;
            Q8=makeQuery(id+"F1.imprint","IMPRINT",FACE,{"disambiguationData":[TD([[makeQuery(id+"F1.imprint","IMPRINT",EDGE,{"derivedFrom":sQuery(id+"F1.wireOp",EDGE,"8a604169-f9db-4d10-b6de-17cdce77b9ee2.MirrorCS")}),-1.0]])]});
            var Q9;
            Q9=makeQuery(id+"F1.imprint","IMPRINT",FACE,{"disambiguationData":[TD([[makeQuery(id+"F1.imprint","IMPRINT",EDGE,{"derivedFrom":sQuery(id+"F1.wireOp",EDGE,"8a604169-f9db-4d10-b6de-17cdce77b9ee7.MirrorCS")}),1.0]])]});
            var Q10;
            Q10=makeQuery(id+"F1.imprint","IMPRINT",FACE,{"disambiguationData":[TD([[makeQuery(id+"F1.imprint","IMPRINT",EDGE,{"derivedFrom":sQuery(id+"F1.wireOp",EDGE,"8a604169-f9db-4d10-b6de-17cdce77b9ee4.MirrorCS")}),-1.0]])]});
            var Q11;
            Q11=makeQuery(id+"F1.imprint","IMPRINT",FACE,{"disambiguationData":[TD([[makeQuery(id+"F1.imprint","IMPRINT",EDGE,{"derivedFrom":sQuery(id+"F1.wireOp",EDGE,"8a604169-f9db-4d10-b6de-17cdce77b9ee6.MirrorCS")}),1.0]])]});
            var Q12;
            Q12=makeQuery(id+"F1.imprint","IMPRINT",FACE,{"disambiguationData":[TD([[makeQuery(id+"F1.imprint","IMPRINT",EDGE,{"derivedFrom":sQuery(id+"F1.wireOp",EDGE,"8a604169-f9db-4d10-b6de-17cdce77b9ee1.MirrorCS")}),1.0]])]});
            var Q13;
            Q13=makeQuery(id+"F1.imprint","IMPRINT",FACE,{"disambiguationData":[TD([[makeQuery(id+"F1.imprint","IMPRINT",EDGE,{"derivedFrom":sQuery(id+"F1.wireOp",EDGE,"8a604169-f9db-4d10-b6de-17cdce77b9ee11.MirrorCS")}),1.0]])]});
            var Q14;
            Q14=makeQuery(id+"F1.imprint","IMPRINT",FACE,{"disambiguationData":[TD([[makeQuery(id+"F1.imprint","IMPRINT",EDGE,{"derivedFrom":sQuery(id+"F1.wireOp",EDGE,"2bd68e58-e41e-494a-8911-974b16a43e85.bottom")}),1.0]])]});
            var Q15;
            Q15=makeQuery(id+"F1.imprint","IMPRINT",FACE,{"disambiguationData":[TD([[makeQuery(id+"F1.imprint","IMPRINT",EDGE,{"derivedFrom":sQuery(id+"F1.wireOp",EDGE,"ef449be0-296d-467a-9b3b-92f5416e835a13.MirrorCS")}),1.0]])]});
            var Q16;
            Q16=makeQuery(id+"F1.imprint","IMPRINT",FACE,{"disambiguationData":[TD([[makeQuery(id+"F1.imprint","IMPRINT",EDGE,{"derivedFrom":sQuery(id+"F1.wireOp",EDGE,"ef449be0-296d-467a-9b3b-92f5416e835a5.MirrorCS")}),-1.0]])]});
            var Q17;
            Q17=makeQuery(id+"F1.imprint","IMPRINT",FACE,{"disambiguationData":[TD([[makeQuery(id+"F1.imprint","IMPRINT",EDGE,{"derivedFrom":sQuery(id+"F1.wireOp",EDGE,"ef449be0-296d-467a-9b3b-92f5416e835a1.MirrorCS")}),-1.0]])]});
            var Q18;
            Q18=makeQuery(id+"F1.imprint","IMPRINT",FACE,{"disambiguationData":[TD([[makeQuery(id+"F1.imprint","IMPRINT",EDGE,{"derivedFrom":sQuery(id+"F1.wireOp",EDGE,"ef449be0-296d-467a-9b3b-92f5416e835a6.MirrorCS")}),-1.0]])]});
            var Q19;
            Q19=makeQuery(id+"F1.imprint","IMPRINT",FACE,{"disambiguationData":[TD([[makeQuery(id+"F1.imprint","IMPRINT",EDGE,{"derivedFrom":sQuery(id+"F1.wireOp",EDGE,"ef449be0-296d-467a-9b3b-92f5416e835a8.MirrorCS")}),-1.0]])]});
            var Q20;
            Q20=makeQuery(id+"F1.imprint","IMPRINT",FACE,{"disambiguationData":[TD([[makeQuery(id+"F1.imprint","IMPRINT",EDGE,{"derivedFrom":sQuery(id+"F1.wireOp",EDGE,"ef449be0-296d-467a-9b3b-92f5416e835a15.MirrorCS")}),-1.0]])]});
            var Q21;
            Q21=makeQuery(id+"F1.imprint","IMPRINT",FACE,{"disambiguationData":[TD([[makeQuery(id+"F1.imprint","IMPRINT",EDGE,{"derivedFrom":sQuery(id+"F1.wireOp",EDGE,"d6889f29-3aff-4a43-887b-f05846102f70.bottom")}),1.0]])]});
            var Q22;
            Q22=makeQuery(id+"F1.imprint","IMPRINT",FACE,{"disambiguationData":[TD([[makeQuery(id+"F1.imprint","IMPRINT",EDGE,{"derivedFrom":sQuery(id+"F1.wireOp",EDGE,"3edb70b5-b804-4be9-ab85-b3a438d2129227.MirrorCS")}),1.0]])]});
            var Q23;
            Q23=makeQuery(id+"F1.imprint","IMPRINT",FACE,{"disambiguationData":[TD([[makeQuery(id+"F1.imprint","IMPRINT",EDGE,{"derivedFrom":sQuery(id+"F1.wireOp",EDGE,"3edb70b5-b804-4be9-ab85-b3a438d212923.MirrorCS")}),1.0]])]});
            var Q24;
            Q24=makeQuery(id+"F1.imprint","IMPRINT",FACE,{"disambiguationData":[TD([[makeQuery(id+"F1.imprint","IMPRINT",EDGE,{"derivedFrom":sQuery(id+"F1.wireOp",EDGE,"3edb70b5-b804-4be9-ab85-b3a438d2129214.MirrorCS")}),1.0]])]});
            var Q25;
            Q25=makeQuery(id+"F1.imprint","IMPRINT",FACE,{"disambiguationData":[TD([[makeQuery(id+"F1.imprint","IMPRINT",EDGE,{"derivedFrom":sQuery(id+"F1.wireOp",EDGE,"3edb70b5-b804-4be9-ab85-b3a438d212922.MirrorCS")}),1.0]])]});
            var Q26;
            Q26=makeQuery(id+"F1.imprint","IMPRINT",FACE,{"disambiguationData":[TD([[makeQuery(id+"F1.imprint","IMPRINT",EDGE,{"derivedFrom":sQuery(id+"F1.wireOp",EDGE,"3edb70b5-b804-4be9-ab85-b3a438d2129216.MirrorCS")}),1.0]])]});
            var Q27;
            Q27=makeQuery(id+"F1.imprint","IMPRINT",FACE,{"disambiguationData":[TD([[makeQuery(id+"F1.imprint","IMPRINT",EDGE,{"derivedFrom":sQuery(id+"F1.wireOp",EDGE,"3edb70b5-b804-4be9-ab85-b3a438d2129232.MirrorCS")}),-1.0]])]});
            var Q28;
            {var subQ3=sQuery(id+"F1.wireOp",EDGE,"767c3735-2e18-495c-a88c-5e601239b8bc.left");Q28=makeQuery(id+"F1.imprint","IMPRINT",FACE,{"disambiguationData":[TD([[makeQuery(id+"F1.imprint","IMPRINT",EDGE,{"derivedFrom":subQ3}),-1.0]])]});}
            var Q29;
            {var subQ0=sQuery(id+"F1.wireOp",EDGE,"767c3735-2e18-495c-a88c-5e601239b8bc.right");Q29=makeQuery(id+"F1.imprint","IMPRINT",FACE,{"disambiguationData":[TD([[makeQuery(id+"F1.imprint","IMPRINT",EDGE,{"derivedFrom":subQ0}),1.0]])]});}
            var Q30;
            Q30=makeQuery(id+"F1.imprint","IMPRINT",FACE,{"disambiguationData":[TD([[makeQuery(id+"F1.imprint","IMPRINT",EDGE,{"derivedFrom":sQuery(id+"F1.wireOp",EDGE,"3edb70b5-b804-4be9-ab85-b3a438d2129229.MirrorCS")}),-1.0]])]});
            var Q31;
            Q31=makeQuery(id+"F1.imprint","IMPRINT",FACE,{"disambiguationData":[TD([[makeQuery(id+"F1.imprint","IMPRINT",EDGE,{"derivedFrom":sQuery(id+"F1.wireOp",EDGE,"3edb70b5-b804-4be9-ab85-b3a438d212921.MirrorCS")}),-1.0]])]});
            var Q32;
            Q32=makeQuery(id+"F1.imprint","IMPRINT",FACE,{"disambiguationData":[TD([[makeQuery(id+"F1.imprint","IMPRINT",EDGE,{"derivedFrom":sQuery(id+"F1.wireOp",EDGE,"3edb70b5-b804-4be9-ab85-b3a438d2129215.MirrorCS")}),-1.0]])]});
            var Q33;
            Q33=makeQuery(id+"F1.imprint","IMPRINT",FACE,{"disambiguationData":[TD([[makeQuery(id+"F1.imprint","IMPRINT",EDGE,{"derivedFrom":sQuery(id+"F1.wireOp",EDGE,"3edb70b5-b804-4be9-ab85-b3a438d2129220.MirrorCS")}),-1.0]])]});
            var Q34;
            Q34=makeQuery(id+"F1.imprint","IMPRINT",FACE,{"disambiguationData":[TD([[makeQuery(id+"F1.imprint","IMPRINT",EDGE,{"derivedFrom":sQuery(id+"F1.wireOp",EDGE,"3edb70b5-b804-4be9-ab85-b3a438d212927.MirrorCS")}),-1.0]])]});
            var Q35;
            Q35=makeQuery(id+"F1.imprint","IMPRINT",FACE,{"disambiguationData":[TD([[makeQuery(id+"F1.imprint","IMPRINT",EDGE,{"derivedFrom":sQuery(id+"F1.wireOp",EDGE,"3edb70b5-b804-4be9-ab85-b3a438d2129228.MirrorCS")}),1.0]])]});
            var Q36;
            {var subQ3=sQuery(id+"F1.wireOp",EDGE,"543f3bcf-fd4b-4987-a5e7-407be729de0d0.MirrorCS");Q36=makeQuery(id+"F1.imprint","IMPRINT",FACE,{"disambiguationData":[TD([[makeQuery(id+"F1.imprint","IMPRINT",EDGE,{"derivedFrom":subQ3}),-1.0]])]});}
            var Q37;
            {var subQ1=sQuery(id+"F1.wireOp",EDGE,"ccf9539e-e2bb-4c1d-8ae2-5d85fc4c74a40.MirrorCS");Q37=makeQuery(id+"F1.imprint","IMPRINT",FACE,{"disambiguationData":[TD([[makeQuery(id+"F1.imprint","IMPRINT",EDGE,{"derivedFrom":subQ1}),1.0]])]});}
            var Q38;
            Q38=makeQuery(id+"F1.imprint","IMPRINT",FACE,{"disambiguationData":[TD([[makeQuery(id+"F1.imprint","IMPRINT",EDGE,{"derivedFrom":sQuery(id+"F1.wireOp",EDGE,"3edb70b5-b804-4be9-ab85-b3a438d2129251.MirrorCS")}),-1.0]])]});
            var Q39;
            Q39=makeQuery(id+"F1.imprint","IMPRINT",FACE,{"disambiguationData":[TD([[makeQuery(id+"F1.imprint","IMPRINT",EDGE,{"derivedFrom":sQuery(id+"F1.wireOp",EDGE,"3edb70b5-b804-4be9-ab85-b3a438d2129211.MirrorCS")}),1.0]])]});
            var Q40;
            Q40=makeQuery(id+"F1.imprint","IMPRINT",FACE,{"disambiguationData":[TD([[makeQuery(id+"F1.imprint","IMPRINT",EDGE,{"derivedFrom":sQuery(id+"F1.wireOp",EDGE,"3edb70b5-b804-4be9-ab85-b3a438d2129226.MirrorCS")}),1.0]])]});
            var Q41;
            Q41=makeQuery(id+"F1.imprint","IMPRINT",FACE,{"disambiguationData":[TD([[makeQuery(id+"F1.imprint","IMPRINT",EDGE,{"derivedFrom":sQuery(id+"F1.wireOp",EDGE,"3edb70b5-b804-4be9-ab85-b3a438d2129218.MirrorCS")}),1.0]])]});
            var Q42;
            Q42=makeQuery(id+"F1.imprint","IMPRINT",FACE,{"disambiguationData":[TD([[makeQuery(id+"F1.imprint","IMPRINT",EDGE,{"derivedFrom":sQuery(id+"F1.wireOp",EDGE,"3edb70b5-b804-4be9-ab85-b3a438d2129225.MirrorCS")}),1.0]])]});
            var Q43;
            Q43=makeQuery(id+"F1.imprint","IMPRINT",FACE,{"disambiguationData":[TD([[makeQuery(id+"F1.imprint","IMPRINT",EDGE,{"derivedFrom":sQuery(id+"F1.wireOp",EDGE,"3edb70b5-b804-4be9-ab85-b3a438d2129263.MirrorCS")}),-1.0]])]});
            var Q44;
            Q44=makeQuery(id+"F1.imprint","IMPRINT",FACE,{"disambiguationData":[TD([[makeQuery(id+"F1.imprint","IMPRINT",EDGE,{"derivedFrom":sQuery(id+"F1.wireOp",EDGE,"6148efe5-7769-4a6e-beb2-6f02e7a2884e0.MirrorCS")}),1.0]])]});
            var Q45;
            Q45=makeQuery(id+"F1.imprint","IMPRINT",FACE,{"disambiguationData":[TD([[makeQuery(id+"F1.imprint","IMPRINT",EDGE,{"derivedFrom":sQuery(id+"F1.wireOp",EDGE,"14cc3a12-7d66-4c02-94a9-419769d5725533.MirrorCS")}),-1.0]])]});
            var Q46;
            Q46=makeQuery(id+"F1.imprint","IMPRINT",FACE,{"disambiguationData":[TD([[makeQuery(id+"F1.imprint","IMPRINT",EDGE,{"derivedFrom":sQuery(id+"F1.wireOp",EDGE,"14cc3a12-7d66-4c02-94a9-419769d572550.MirrorCS")}),-1.0]])]});
            var Q47;
            Q47=makeQuery(id+"F1.imprint","IMPRINT",FACE,{"disambiguationData":[TD([[makeQuery(id+"F1.imprint","IMPRINT",EDGE,{"derivedFrom":sQuery(id+"F1.wireOp",EDGE,"14cc3a12-7d66-4c02-94a9-419769d572558.MirrorCS")}),-1.0]])]});
            var Q48;
            Q48=makeQuery(id+"F1.imprint","IMPRINT",FACE,{"disambiguationData":[TD([[makeQuery(id+"F1.imprint","IMPRINT",EDGE,{"derivedFrom":sQuery(id+"F1.wireOp",EDGE,"14cc3a12-7d66-4c02-94a9-419769d5725514.MirrorCS")}),-1.0]])]});
            var Q49;
            Q49=makeQuery(id+"F1.imprint","IMPRINT",FACE,{"disambiguationData":[TD([[makeQuery(id+"F1.imprint","IMPRINT",EDGE,{"derivedFrom":sQuery(id+"F1.wireOp",EDGE,"14cc3a12-7d66-4c02-94a9-419769d5725517.MirrorCS")}),-1.0]])]});
            var Q50;
            Q50=makeQuery(id+"F1.imprint","IMPRINT",FACE,{"disambiguationData":[TD([[makeQuery(id+"F1.imprint","IMPRINT",EDGE,{"derivedFrom":sQuery(id+"F1.wireOp",EDGE,"14cc3a12-7d66-4c02-94a9-419769d5725522.MirrorCS")}),-1.0]])]});
            var Q51;
            {var subQ1=sQuery(id+"F1.wireOp",EDGE,"64f74f13-c9d3-42ce-b6e6-9e83b05c69170.MirrorCS");Q51=makeQuery(id+"F1.imprint","IMPRINT",FACE,{"disambiguationData":[TD([[makeQuery(id+"F1.imprint","IMPRINT",EDGE,{"derivedFrom":subQ1}),-1.0]])]});}
            var Q52;
            {var subQ3=sQuery(id+"F1.wireOp",EDGE,"b25d534e-4642-4852-ae6d-545176e5d0d50.MirrorCS");Q52=makeQuery(id+"F1.imprint","IMPRINT",FACE,{"disambiguationData":[TD([[makeQuery(id+"F1.imprint","IMPRINT",EDGE,{"derivedFrom":subQ3}),1.0]])]});}
            var Q53;
            Q53=makeQuery(id+"F1.imprint","IMPRINT",FACE,{"disambiguationData":[TD([[makeQuery(id+"F1.imprint","IMPRINT",EDGE,{"derivedFrom":sQuery(id+"F1.wireOp",EDGE,"14cc3a12-7d66-4c02-94a9-419769d5725521.MirrorCS")}),1.0]])]});
            var Q54;
            Q54=makeQuery(id+"F1.imprint","IMPRINT",FACE,{"disambiguationData":[TD([[makeQuery(id+"F1.imprint","IMPRINT",EDGE,{"derivedFrom":sQuery(id+"F1.wireOp",EDGE,"14cc3a12-7d66-4c02-94a9-419769d572553.MirrorCS")}),1.0]])]});
            var Q55;
            Q55=makeQuery(id+"F1.imprint","IMPRINT",FACE,{"disambiguationData":[TD([[makeQuery(id+"F1.imprint","IMPRINT",EDGE,{"derivedFrom":sQuery(id+"F1.wireOp",EDGE,"14cc3a12-7d66-4c02-94a9-419769d572557.MirrorCS")}),1.0]])]});
            var Q56;
            Q56=makeQuery(id+"F1.imprint","IMPRINT",FACE,{"disambiguationData":[TD([[makeQuery(id+"F1.imprint","IMPRINT",EDGE,{"derivedFrom":sQuery(id+"F1.wireOp",EDGE,"14cc3a12-7d66-4c02-94a9-419769d5725512.MirrorCS")}),1.0]])]});
            var Q57;
            Q57=makeQuery(id+"F1.imprint","IMPRINT",FACE,{"disambiguationData":[TD([[makeQuery(id+"F1.imprint","IMPRINT",EDGE,{"derivedFrom":sQuery(id+"F1.wireOp",EDGE,"14cc3a12-7d66-4c02-94a9-419769d5725515.MirrorCS")}),1.0]])]});
            var Q58;
            Q58=makeQuery(id+"F1.imprint","IMPRINT",FACE,{"disambiguationData":[TD([[makeQuery(id+"F1.imprint","IMPRINT",EDGE,{"derivedFrom":sQuery(id+"F1.wireOp",EDGE,"14cc3a12-7d66-4c02-94a9-419769d5725527.MirrorCS")}),-1.0]])]});
            var Q59;
            Q59=makeQuery(id+"F1.imprint","IMPRINT",FACE,{"disambiguationData":[TD([[makeQuery(id+"F1.imprint","IMPRINT",EDGE,{"derivedFrom":sQuery(id+"F1.wireOp",EDGE,"E52.MirrorCS")}),1.0]])]});
            var Q60;
            Q60=makeQuery(id+"F1.imprint","IMPRINT",FACE,{"disambiguationData":[TD([[makeQuery(id+"F1.imprint","IMPRINT",EDGE,{"derivedFrom":sQuery(id+"F1.wireOp",EDGE,"25976770-79ef-484a-9ccd-48a8619e55600.MirrorCS")}),-1.0]])]});
            var Q61;
            Q61=makeQuery(id+"F1.imprint","IMPRINT",FACE,{"disambiguationData":[TD([[makeQuery(id+"F1.imprint","IMPRINT",EDGE,{"derivedFrom":sQuery(id+"F1.wireOp",EDGE,"25976770-79ef-484a-9ccd-48a8619e55601.MirrorCS")}),1.0]])]});
            var Q62;
            Q62=makeQuery(id+"F1.imprint","IMPRINT",FACE,{"disambiguationData":[TD([[makeQuery(id+"F1.imprint","IMPRINT",EDGE,{"derivedFrom":sQuery(id+"F1.wireOp",EDGE,"25976770-79ef-484a-9ccd-48a8619e55602.MirrorCS")}),1.0]])]});
            var Q63;
            Q63=makeQuery(id+"F1.imprint","IMPRINT",FACE,{"disambiguationData":[TD([[makeQuery(id+"F1.imprint","IMPRINT",EDGE,{"derivedFrom":sQuery(id+"F1.wireOp",EDGE,"25976770-79ef-484a-9ccd-48a8619e55603.MirrorCS")}),1.0]])]});
            var Q64;
            Q64=makeQuery(id+"F1.imprint","IMPRINT",FACE,{"disambiguationData":[TD([[makeQuery(id+"F1.imprint","IMPRINT",EDGE,{"derivedFrom":sQuery(id+"F1.wireOp",EDGE,"885c739e-fade-46be-8644-c01cf5765c607.MirrorCS")}),1.0]])]});
            var Q65;
            Q65=makeQuery(id+"F1.imprint","IMPRINT",FACE,{"disambiguationData":[TD([[makeQuery(id+"F1.imprint","IMPRINT",EDGE,{"derivedFrom":sQuery(id+"F1.wireOp",EDGE,"885c739e-fade-46be-8644-c01cf5765c604.MirrorCS")}),-1.0]])]});
            var Q66;
            Q66=makeQuery(id+"F1.imprint","IMPRINT",FACE,{"disambiguationData":[TD([[makeQuery(id+"F1.imprint","IMPRINT",EDGE,{"derivedFrom":sQuery(id+"F1.wireOp",EDGE,"885c739e-fade-46be-8644-c01cf5765c601.MirrorCS")}),-1.0]])]});
            var Q67;
            Q67=makeQuery(id+"F1.imprint","IMPRINT",FACE,{"disambiguationData":[TD([[makeQuery(id+"F1.imprint","IMPRINT",EDGE,{"derivedFrom":sQuery(id+"F1.wireOp",EDGE,"885c739e-fade-46be-8644-c01cf5765c603.MirrorCS")}),1.0]])]});
            var Q68;
            Q68=makeQuery(id+"F1.imprint","IMPRINT",FACE,{"disambiguationData":[TD([[makeQuery(id+"F1.imprint","IMPRINT",EDGE,{"derivedFrom":sQuery(id+"F1.wireOp",EDGE,"E72.bottom")}),-1.0]])]});
            var Q69;
            Q69=makeQuery(id+"F1.imprint","IMPRINT",FACE,{"disambiguationData":[TD([[makeQuery(id+"F1.imprint","IMPRINT",EDGE,{"derivedFrom":sQuery(id+"F1.wireOp",EDGE,"E58.MirrorCS")}),-1.0]])]});
            var Q70;
            Q70=makeQuery(id+"F1.imprint","IMPRINT",FACE,{"disambiguationData":[TD([[makeQuery(id+"F1.imprint","IMPRINT",EDGE,{"derivedFrom":sQuery(id+"F1.wireOp",EDGE,"7d95df49-463f-4ad9-b0a5-1613ba3352754.MirrorCS")}),1.0]])]});
            var Q71;
            Q71=makeQuery(id+"F1.imprint","IMPRINT",FACE,{"disambiguationData":[TD([[makeQuery(id+"F1.imprint","IMPRINT",EDGE,{"derivedFrom":sQuery(id+"F1.wireOp",EDGE,"7d95df49-463f-4ad9-b0a5-1613ba3352751.MirrorCS")}),-1.0]])]});
            var Q72;
            Q72=makeQuery(id+"F1.imprint","IMPRINT",FACE,{"disambiguationData":[TD([[makeQuery(id+"F1.imprint","IMPRINT",EDGE,{"derivedFrom":sQuery(id+"F1.wireOp",EDGE,"7d95df49-463f-4ad9-b0a5-1613ba3352755.MirrorCS")}),1.0]])]});
            var Q73;
            Q73=makeQuery(id+"F1.imprint","IMPRINT",FACE,{"disambiguationData":[TD([[makeQuery(id+"F1.imprint","IMPRINT",EDGE,{"derivedFrom":sQuery(id+"F1.wireOp",EDGE,"7d95df49-463f-4ad9-b0a5-1613ba3352752.MirrorCS")}),1.0]])]});
            var Q74;
            {var subQ5=sQuery(id+"F1.wireOp",EDGE,"E74.MirrorCS");Q74=makeQuery(id+"F1.imprint","IMPRINT",FACE,{"disambiguationData":[TD([[makeQuery(id+"F1.imprint","IMPRINT",EDGE,{"derivedFrom":subQ5}),-1.0]])]});}
            var Q75;
            Q75=makeQuery(id+"F1.imprint","IMPRINT",FACE,{"disambiguationData":[TD([[makeQuery(id+"F1.imprint","IMPRINT",EDGE,{"derivedFrom":sQuery(id+"F1.wireOp",EDGE,"c779b952-6aee-4fca-9f93-b55e32f81f0d6.MirrorCS")}),-1.0]])]});
            var Q76;
            Q76=makeQuery(id+"F1.imprint","IMPRINT",FACE,{"disambiguationData":[TD([[makeQuery(id+"F1.imprint","IMPRINT",EDGE,{"derivedFrom":sQuery(id+"F1.wireOp",EDGE,"c779b952-6aee-4fca-9f93-b55e32f81f0d2.MirrorCS")}),1.0]])]});
            var Q77;
            Q77=makeQuery(id+"F1.imprint","IMPRINT",FACE,{"disambiguationData":[TD([[makeQuery(id+"F1.imprint","IMPRINT",EDGE,{"derivedFrom":sQuery(id+"F1.wireOp",EDGE,"c779b952-6aee-4fca-9f93-b55e32f81f0d5.MirrorCS")}),-1.0]])]});
            var Q78;
            Q78=makeQuery(id+"F1.imprint","IMPRINT",FACE,{"disambiguationData":[TD([[makeQuery(id+"F1.imprint","IMPRINT",EDGE,{"derivedFrom":sQuery(id+"F1.wireOp",EDGE,"c779b952-6aee-4fca-9f93-b55e32f81f0d7.MirrorCS")}),1.0]])]});
            var Q79;
            {var subQ5=sQuery(id+"F1.wireOp",EDGE,"E69.MirrorCS");Q79=makeQuery(id+"F1.imprint","IMPRINT",FACE,{"disambiguationData":[TD([[makeQuery(id+"F1.imprint","IMPRINT",EDGE,{"derivedFrom":subQ5}),1.0]])]});}
            var Q80;
            {var subQ5=sQuery(id+"F1.wireOp",EDGE,"E64.MirrorCS");Q80=makeQuery(id+"F1.imprint","IMPRINT",FACE,{"disambiguationData":[TD([[makeQuery(id+"F1.imprint","IMPRINT",EDGE,{"derivedFrom":subQ5}),1.0]])]});}
            var Q81;
            Q81=makeQuery(id+"F1.imprint","IMPRINT",FACE,{"disambiguationData":[TD([[makeQuery(id+"F1.imprint","IMPRINT",EDGE,{"derivedFrom":sQuery(id+"F1.wireOp",EDGE,"21633593-0eae-4d39-86c1-0caeb0c5c4267.MirrorCS")}),-1.0]])]});
            var Q82;
            Q82=makeQuery(id+"F1.imprint","IMPRINT",FACE,{"disambiguationData":[TD([[makeQuery(id+"F1.imprint","IMPRINT",EDGE,{"derivedFrom":sQuery(id+"F1.wireOp",EDGE,"21633593-0eae-4d39-86c1-0caeb0c5c4262.MirrorCS")}),-1.0]])]});
            var Q83;
            Q83=makeQuery(id+"F1.imprint","IMPRINT",FACE,{"disambiguationData":[TD([[makeQuery(id+"F1.imprint","IMPRINT",EDGE,{"derivedFrom":sQuery(id+"F1.wireOp",EDGE,"21633593-0eae-4d39-86c1-0caeb0c5c4263.MirrorCS")}),-1.0]])]});
            var Q84;
            Q84=makeQuery(id+"F1.imprint","IMPRINT",FACE,{"disambiguationData":[TD([[makeQuery(id+"F1.imprint","IMPRINT",EDGE,{"derivedFrom":sQuery(id+"F1.wireOp",EDGE,"21633593-0eae-4d39-86c1-0caeb0c5c4265.MirrorCS")}),1.0]])]});
            var Q85;
            Q85=makeQuery(id+"F1.imprint","IMPRINT",FACE,{"disambiguationData":[TD([[makeQuery(id+"F1.imprint","IMPRINT",EDGE,{"derivedFrom":sQuery(id+"F1.wireOp",EDGE,"b1003afd-8adf-4a9f-9a0a-5e0e458732772.MirrorCS")}),1.0]])]});
            var Q86;
            {var subQ5=sQuery(id+"F1.wireOp",EDGE,"E70.MirrorCS");Q86=makeQuery(id+"F1.imprint","IMPRINT",FACE,{"disambiguationData":[TD([[makeQuery(id+"F1.imprint","IMPRINT",EDGE,{"derivedFrom":subQ5}),-1.0]])]});}
            var Q87;
            {var subQ5=sQuery(id+"F1.wireOp",EDGE,"E76.MirrorCS");Q87=makeQuery(id+"F1.imprint","IMPRINT",FACE,{"disambiguationData":[TD([[makeQuery(id+"F1.imprint","IMPRINT",EDGE,{"derivedFrom":subQ5}),1.0]])]});}
            var Q88;
            Q88=makeQuery(id+"F1.imprint","IMPRINT",FACE,{"disambiguationData":[TD([[makeQuery(id+"F1.imprint","IMPRINT",EDGE,{"derivedFrom":sQuery(id+"F1.wireOp",EDGE,"0d878c01-ef83-44ce-939f-d22243e972b44.MirrorCS")}),-1.0]])]});
            var Q89;
            Q89=makeQuery(id+"F1.imprint","IMPRINT",FACE,{"disambiguationData":[TD([[makeQuery(id+"F1.imprint","IMPRINT",EDGE,{"derivedFrom":sQuery(id+"F1.wireOp",EDGE,"0d878c01-ef83-44ce-939f-d22243e972b45.MirrorCS")}),1.0]])]});
            var Q90;
            Q90=makeQuery(id+"F1.imprint","IMPRINT",FACE,{"disambiguationData":[TD([[makeQuery(id+"F1.imprint","IMPRINT",EDGE,{"derivedFrom":sQuery(id+"F1.wireOp",EDGE,"0d878c01-ef83-44ce-939f-d22243e972b43.MirrorCS")}),-1.0]])]});
            var Q91;
            Q91=makeQuery(id+"F1.imprint","IMPRINT",FACE,{"disambiguationData":[TD([[makeQuery(id+"F1.imprint","IMPRINT",EDGE,{"derivedFrom":sQuery(id+"F1.wireOp",EDGE,"E682.MirrorCS")}),1.0]])]});
            var Q92;
            Q92=makeQuery(id+"F1.imprint","IMPRINT",FACE,{"disambiguationData":[TD([[makeQuery(id+"F1.imprint","IMPRINT",EDGE,{"derivedFrom":sQuery(id+"F1.wireOp",EDGE,"E77.MirrorCS")}),-1.0]])]});
            var Q93;
            Q93=makeQuery(id+"F1.imprint","IMPRINT",FACE,{"disambiguationData":[TD([[makeQuery(id+"F1.imprint","IMPRINT",EDGE,{"derivedFrom":sQuery(id+"F1.wireOp",EDGE,"b1003afd-8adf-4a9f-9a0a-5e0e458732775.MirrorCS")}),-1.0]])]});
            var Q94;
            Q94=makeQuery(id+"F1.imprint","IMPRINT",FACE,{"disambiguationData":[TD([[makeQuery(id+"F1.imprint","IMPRINT",EDGE,{"derivedFrom":sQuery(id+"F1.wireOp",EDGE,"b1003afd-8adf-4a9f-9a0a-5e0e458732770.MirrorCS")}),1.0]])]});
            var Q95;
            Q95=makeQuery(id+"F1.imprint","IMPRINT",FACE,{"disambiguationData":[TD([[makeQuery(id+"F1.imprint","IMPRINT",EDGE,{"derivedFrom":sQuery(id+"F1.wireOp",EDGE,"b1003afd-8adf-4a9f-9a0a-5e0e458732771.MirrorCS")}),1.0]])]});
            var Q96;
            Q96=makeQuery(id+"F1.imprint","IMPRINT",FACE,{"disambiguationData":[TD([[makeQuery(id+"F1.imprint","IMPRINT",EDGE,{"derivedFrom":sQuery(id+"F1.wireOp",EDGE,"E116.MirrorCS")}),1.0]])]});
            var Q97;
            Q97=makeQuery(id+"F1.imprint","IMPRINT",FACE,{"disambiguationData":[TD([[makeQuery(id+"F1.imprint","IMPRINT",EDGE,{"derivedFrom":sQuery(id+"F1.wireOp",EDGE,"E108.MirrorCS")}),1.0]])]});
            var Q98;
            Q98=makeQuery(id+"F1.imprint","IMPRINT",FACE,{"disambiguationData":[TD([[makeQuery(id+"F1.imprint","IMPRINT",EDGE,{"derivedFrom":sQuery(id+"F1.wireOp",EDGE,"E102.MirrorCS")}),-1.0]])]});
            var Q99;
            Q99=makeQuery(id+"F1.imprint","IMPRINT",FACE,{"disambiguationData":[TD([[makeQuery(id+"F1.imprint","IMPRINT",EDGE,{"derivedFrom":sQuery(id+"F1.wireOp",EDGE,"E110.MirrorCS")}),1.0]])]});
            var Q100;
            Q100=makeQuery(id+"F1.imprint","IMPRINT",FACE,{"disambiguationData":[TD([[makeQuery(id+"F1.imprint","IMPRINT",EDGE,{"derivedFrom":sQuery(id+"F1.wireOp",EDGE,"E226.MirrorCS")}),1.0]])]});
            var Q101;
            {var subQ5=sQuery(id+"F1.wireOp",EDGE,"E65.MirrorCS");Q101=makeQuery(id+"F1.imprint","IMPRINT",FACE,{"disambiguationData":[TD([[makeQuery(id+"F1.imprint","IMPRINT",EDGE,{"derivedFrom":subQ5}),-1.0]])]});}
            var Q102;
            Q102=makeQuery(id+"F1.imprint","IMPRINT",FACE,{"disambiguationData":[TD([[makeQuery(id+"F1.imprint","IMPRINT",EDGE,{"derivedFrom":sQuery(id+"F1.wireOp",EDGE,"E218.MirrorCS")}),1.0]])]});
            var Q103;
            Q103=makeQuery(id+"F1.imprint","IMPRINT",FACE,{"disambiguationData":[TD([[makeQuery(id+"F1.imprint","IMPRINT",EDGE,{"derivedFrom":sQuery(id+"F1.wireOp",EDGE,"E219.MirrorCS")}),1.0]])]});
            var Q104;
            Q104=makeQuery(id+"F1.imprint","IMPRINT",FACE,{"disambiguationData":[TD([[makeQuery(id+"F1.imprint","IMPRINT",EDGE,{"derivedFrom":sQuery(id+"F1.wireOp",EDGE,"E223.MirrorCS")}),1.0]])]});
            var Q105;
            Q105=makeQuery(id+"F1.imprint","IMPRINT",FACE,{"disambiguationData":[TD([[makeQuery(id+"F1.imprint","IMPRINT",EDGE,{"derivedFrom":sQuery(id+"F1.wireOp",EDGE,"E203.MirrorCS")}),1.0]])]});
            var Q106;
            Q106=makeQuery(id+"F1.imprint","IMPRINT",FACE,{"disambiguationData":[TD([[makeQuery(id+"F1.imprint","IMPRINT",EDGE,{"derivedFrom":sQuery(id+"F1.wireOp",EDGE,"E209.MirrorCS")}),-1.0]])]});
            var Q107;
            Q107=makeQuery(id+"F1.imprint","IMPRINT",FACE,{"disambiguationData":[TD([[makeQuery(id+"F1.imprint","IMPRINT",EDGE,{"derivedFrom":sQuery(id+"F1.wireOp",EDGE,"E202.MirrorCS")}),-1.0]])]});
            var Q108;
            Q108=makeQuery(id+"F1.imprint","IMPRINT",FACE,{"disambiguationData":[TD([[makeQuery(id+"F1.imprint","IMPRINT",EDGE,{"derivedFrom":sQuery(id+"F1.wireOp",EDGE,"E205.MirrorCS")}),-1.0]])]});
            var Q109;
            Q109=makeQuery(id+"F1.imprint","IMPRINT",FACE,{"disambiguationData":[TD([[makeQuery(id+"F1.imprint","IMPRINT",EDGE,{"derivedFrom":sQuery(id+"F1.wireOp",EDGE,"E186.MirrorCS")}),1.0]])]});
            var Q110;
            Q110=makeQuery(id+"F1.imprint","IMPRINT",FACE,{"disambiguationData":[TD([[makeQuery(id+"F1.imprint","IMPRINT",EDGE,{"derivedFrom":sQuery(id+"F1.wireOp",EDGE,"E184.MirrorCS")}),1.0]])]});
            var Q111;
            Q111=makeQuery(id+"F1.imprint","IMPRINT",FACE,{"disambiguationData":[TD([[makeQuery(id+"F1.imprint","IMPRINT",EDGE,{"derivedFrom":sQuery(id+"F1.wireOp",EDGE,"E183.MirrorCS")}),1.0]])]});
            var Q112;
            Q112=makeQuery(id+"F1.imprint","IMPRINT",FACE,{"disambiguationData":[TD([[makeQuery(id+"F1.imprint","IMPRINT",EDGE,{"derivedFrom":sQuery(id+"F1.wireOp",EDGE,"E185.MirrorCS")}),1.0]])]});
            var Q113;
            Q113=makeQuery(id+"F1.imprint","IMPRINT",FACE,{"disambiguationData":[TD([[makeQuery(id+"F1.imprint","IMPRINT",EDGE,{"derivedFrom":sQuery(id+"F1.wireOp",EDGE,"E168.MirrorCS")}),1.0]])]});
            var Q114;
            Q114=makeQuery(id+"F1.imprint","IMPRINT",FACE,{"disambiguationData":[TD([[makeQuery(id+"F1.imprint","IMPRINT",EDGE,{"derivedFrom":sQuery(id+"F1.wireOp",EDGE,"E163.MirrorCS")}),-1.0]])]});
            var Q115;
            Q115=makeQuery(id+"F1.imprint","IMPRINT",FACE,{"disambiguationData":[TD([[makeQuery(id+"F1.imprint","IMPRINT",EDGE,{"derivedFrom":sQuery(id+"F1.wireOp",EDGE,"E162.MirrorCS")}),-1.0]])]});
            var Q116;
            Q116=makeQuery(id+"F1.imprint","IMPRINT",FACE,{"disambiguationData":[TD([[makeQuery(id+"F1.imprint","IMPRINT",EDGE,{"derivedFrom":sQuery(id+"F1.wireOp",EDGE,"E166.MirrorCS")}),-1.0]])]});
            var Q117;
            Q117=makeQuery(id+"F1.imprint","IMPRINT",FACE,{"disambiguationData":[TD([[makeQuery(id+"F1.imprint","IMPRINT",EDGE,{"derivedFrom":sQuery(id+"F1.wireOp",EDGE,"E143.MirrorCS")}),1.0]])]});
            var Q118;
            Q118=makeQuery(id+"F1.imprint","IMPRINT",FACE,{"disambiguationData":[TD([[makeQuery(id+"F1.imprint","IMPRINT",EDGE,{"derivedFrom":sQuery(id+"F1.wireOp",EDGE,"E142.MirrorCS")}),1.0]])]});
            var Q119;
            Q119=makeQuery(id+"F1.imprint","IMPRINT",FACE,{"disambiguationData":[TD([[makeQuery(id+"F1.imprint","IMPRINT",EDGE,{"derivedFrom":sQuery(id+"F1.wireOp",EDGE,"E150.MirrorCS")}),1.0]])]});
            var Q120;
            Q120=makeQuery(id+"F1.imprint","IMPRINT",FACE,{"disambiguationData":[TD([[makeQuery(id+"F1.imprint","IMPRINT",EDGE,{"derivedFrom":sQuery(id+"F1.wireOp",EDGE,"E145.MirrorCS")}),1.0]])]});
            var Q121;
            Q121=makeQuery(id+"F1.imprint","IMPRINT",FACE,{"disambiguationData":[TD([[makeQuery(id+"F1.imprint","IMPRINT",EDGE,{"derivedFrom":sQuery(id+"F1.wireOp",EDGE,"E125")}),-1.0]])]});
            var Q122;
            Q122=makeQuery(id+"F1.imprint","IMPRINT",FACE,{"disambiguationData":[TD([[makeQuery(id+"F1.imprint","IMPRINT",EDGE,{"derivedFrom":sQuery(id+"F1.wireOp",EDGE,"E123")}),-1.0]])]});
            var Q123;
            Q123=makeQuery(id+"F1.imprint","IMPRINT",FACE,{"disambiguationData":[TD([[makeQuery(id+"F1.imprint","IMPRINT",EDGE,{"derivedFrom":sQuery(id+"F1.wireOp",EDGE,"E121")}),-1.0]])]});
            var Q124;
            Q124=makeQuery(id+"F1.imprint","IMPRINT",FACE,{"disambiguationData":[TD([[makeQuery(id+"F1.imprint","IMPRINT",EDGE,{"derivedFrom":sQuery(id+"F1.wireOp",EDGE,"E137")}),-1.0]])]});
            var Q125;
            Q125=makeQuery(id+"F1.imprint","IMPRINT",FACE,{"disambiguationData":[TD([[makeQuery(id+"F1.imprint","IMPRINT",EDGE,{"derivedFrom":sQuery(id+"F1.wireOp",EDGE,"E82")}),1.0]])]});
            var Q126;
            Q126=makeQuery(id+"F1.imprint","IMPRINT",FACE,{"disambiguationData":[TD([[makeQuery(id+"F1.imprint","IMPRINT",EDGE,{"derivedFrom":sQuery(id+"F1.wireOp",EDGE,"E84")}),1.0]])]});
            var Q127;
            Q127=makeQuery(id+"F1.imprint","IMPRINT",FACE,{"disambiguationData":[TD([[makeQuery(id+"F1.imprint","IMPRINT",EDGE,{"derivedFrom":sQuery(id+"F1.wireOp",EDGE,"E88")}),1.0]])]});
            var Q128;
            Q128=makeQuery(id+"F1.imprint","IMPRINT",FACE,{"disambiguationData":[TD([[makeQuery(id+"F1.imprint","IMPRINT",EDGE,{"derivedFrom":sQuery(id+"F1.wireOp",EDGE,"E86")}),1.0]])]});
            extrude(context, id + "F4", {"entities" : qUnion([Q0, Q1, Q2, Q3, Q4, Q5, Q6, Q7, Q8, Q9, Q10, Q11, Q12, Q13, Q14, Q15, Q16, Q17, Q18, Q19, Q20, Q21, Q22, Q23, Q24, Q25, Q26, Q27, Q28, Q29, Q30, Q31, Q32, Q33, Q34, Q35, Q36, Q37, Q38, Q39, Q40, Q41, Q42, Q43, Q44, Q45, Q46, Q47, Q48, Q49, Q50, Q51, Q52, Q53, Q54, Q55, Q56, Q57, Q58, Q59, Q60, Q61, Q62, Q63, Q64, Q65, Q66, Q67, Q68, Q69, Q70, Q71, Q72, Q73, Q74, Q75, Q76, Q77, Q78, Q79, Q80, Q81, Q82, Q83, Q84, Q85, Q86, Q87, Q88, Q89, Q90, Q91, Q92, Q93, Q94, Q95, Q96, Q97, Q98, Q99, Q100, Q101, Q102, Q103, Q104, Q105, Q106, Q107, Q108, Q109, Q110, Q111, Q112, Q113, Q114, Q115, Q116, Q117, Q118, Q119, Q120, Q121, Q122, Q123, Q124, Q125, Q126, Q127, Q128]), "operationType" : NewBodyOperationType.REMOVE, "endBound" : BoundingType.THROUGH_ALL, "offsetDistance" : 25 * mm, "depth" : 25 * mm});
        }
        {
            var Q0;
            Q0=makeQuery(id+"F2.imprint","IMPRINT",FACE,{"disambiguationData":[TD([[makeQuery(id+"F2.imprint","IMPRINT",EDGE,{"derivedFrom":sQuery(id+"F2.wireOp",EDGE,"E237.bottom")}),1.0]])]});
            extrude(context, id + "F5", {"entities" : qUnion([Q0]), "offsetDistance" : 25 * mm, "depth" : 23 * mm});
        }
        {
            var Q0;
            Q0=makeQuery(id+"F3.opExtrude","SWEPT_BODY",BODY,{"disambiguationData":[OSD([sQuery(id+"F0.wireOp",EDGE,"E0.bottom"),sQuery(id+"F0.wireOp",EDGE,"E0.top"),sQuery(id+"F0.wireOp",EDGE,"E0.left"),sQuery(id+"F0.wireOp",EDGE,"E0.right"),sQuery(id+"F0.wireOp",EDGE,"E1"),sQuery(id+"F0.wireOp",EDGE,"E2"),sQuery(id+"F0.wireOp",EDGE,"E3"),sQuery(id+"F0.wireOp",EDGE,"E4"),sQuery(id+"F0.wireOp",EDGE,"E5"),sQuery(id+"F0.wireOp",EDGE,"E6"),sQuery(id+"F0.wireOp",EDGE,"E7"),sQuery(id+"F0.wireOp",EDGE,"E8"),sQuery(id+"F0.wireOp",EDGE,"E9"),sQuery(id+"F0.wireOp",EDGE,"E10"),sQuery(id+"F0.wireOp",EDGE,"E11"),sQuery(id+"F0.wireOp",EDGE,"E12"),sQuery(id+"F0.wireOp",EDGE,"E13"),sQuery(id+"F0.wireOp",EDGE,"E14"),sQuery(id+"F0.wireOp",EDGE,"E15"),sQuery(id+"F0.wireOp",EDGE,"E16")])]});
            var Q1;
            Q1=makeQuery(id+"F5.opExtrude","SWEPT_BODY",BODY,{"disambiguationData":[OSD([sQuery(id+"F2.wireOp",EDGE,"E237.bottom"),sQuery(id+"F2.wireOp",EDGE,"E237.top"),sQuery(id+"F2.wireOp",EDGE,"E237.left"),sQuery(id+"F2.wireOp",EDGE,"E237.right")])]});
            booleanBodies(context, id + "F6", {"operationType" : BooleanOperationType.SUBTRACTION, "tools" : qUnion([Q0]), "targets" : qUnion([Q1]), "keepTools" : true});
        }
        {
            var Q0;
            Q0=makeQuery(id+"FsNRKL0DmnP3UvC_2.boolean.opBoolean","MERGE",FACE,{"derivedFrom":[makeQuery(id+"F5.opExtrude","SWEPT_FACE",FACE,{"disambiguationData":[OSD([sQuery(id+"F2.wireOp",EDGE,"E237.top")])]}),makeQuery(id+"FsNRKL0DmnP3UvC_2.opExtrude","SWEPT_FACE",FACE,{"disambiguationData":[OSD([sQuery(id+"F1.wireOp",EDGE,"6a9f6b4e-8c17-479e-95aa-c868ed02bcc8.top")])]}),makeQuery(id+"FsNRKL0DmnP3UvC_2.opExtrude","SWEPT_FACE",FACE,{"disambiguationData":[OSD([sQuery(id+"F1.wireOp",EDGE,"d0e4a734-2a00-432a-b971-5d8aa04fd6d9.top")])]}),makeQuery(id+"FsNRKL0DmnP3UvC_2.opExtrude","SWEPT_FACE",FACE,{"disambiguationData":[OSD([sQuery(id+"F1.wireOp",EDGE,"0fa12c67-d307-4137-8aa7-c6dfb889ed58.top")])]}),makeQuery(id+"FsNRKL0DmnP3UvC_2.opExtrude","SWEPT_FACE",FACE,{"disambiguationData":[OSD([sQuery(id+"F1.wireOp",EDGE,"b24369ca-d6b9-488d-87b8-04e79b56e681.top")])]}),makeQuery(id+"FsNRKL0DmnP3UvC_2.opExtrude","SWEPT_FACE",FACE,{"disambiguationData":[OSD([sQuery(id+"F1.wireOp",EDGE,"bdd40437-d99c-4cb8-ad16-0bfbec51b95a.top")])]}),makeQuery(id+"FsNRKL0DmnP3UvC_2.opExtrude","SWEPT_FACE",FACE,{"disambiguationData":[OSD([sQuery(id+"F1.wireOp",EDGE,"855304bd-eab8-4061-b494-b8053609a213.top")])]}),makeQuery(id+"FsNRKL0DmnP3UvC_2.opExtrude","SWEPT_FACE",FACE,{"disambiguationData":[OSD([sQuery(id+"F1.wireOp",EDGE,"8a604169-f9db-4d10-b6de-17cdce77b9ee7.MirrorCS")])]}),makeQuery(id+"FsNRKL0DmnP3UvC_2.opExtrude","SWEPT_FACE",FACE,{"disambiguationData":[OSD([sQuery(id+"F1.wireOp",EDGE,"8a604169-f9db-4d10-b6de-17cdce77b9ee17.MirrorCS")])]}),makeQuery(id+"FsNRKL0DmnP3UvC_2.opExtrude","SWEPT_FACE",FACE,{"disambiguationData":[OSD([sQuery(id+"F1.wireOp",EDGE,"8a604169-f9db-4d10-b6de-17cdce77b9ee18.MirrorCS")])]}),makeQuery(id+"FsNRKL0DmnP3UvC_2.opExtrude","SWEPT_FACE",FACE,{"disambiguationData":[OSD([sQuery(id+"F1.wireOp",EDGE,"8a604169-f9db-4d10-b6de-17cdce77b9ee20.MirrorCS")])]}),makeQuery(id+"FsNRKL0DmnP3UvC_2.opExtrude","SWEPT_FACE",FACE,{"disambiguationData":[OSD([sQuery(id+"F1.wireOp",EDGE,"8a604169-f9db-4d10-b6de-17cdce77b9ee22.MirrorCS")])]}),makeQuery(id+"FsNRKL0DmnP3UvC_2.opExtrude","SWEPT_FACE",FACE,{"disambiguationData":[OSD([sQuery(id+"F1.wireOp",EDGE,"8a604169-f9db-4d10-b6de-17cdce77b9ee26.MirrorCS")])]}),makeQuery(id+"FsNRKL0DmnP3UvC_2.opExtrude","SWEPT_FACE",FACE,{"disambiguationData":[OSD([sQuery(id+"F1.wireOp",EDGE,"ef449be0-296d-467a-9b3b-92f5416e835a1.MirrorCS")])]}),makeQuery(id+"FsNRKL0DmnP3UvC_2.opExtrude","SWEPT_FACE",FACE,{"disambiguationData":[OSD([sQuery(id+"F1.wireOp",EDGE,"ef449be0-296d-467a-9b3b-92f5416e835a5.MirrorCS")])]}),makeQuery(id+"FsNRKL0DmnP3UvC_2.opExtrude","SWEPT_FACE",FACE,{"disambiguationData":[OSD([sQuery(id+"F1.wireOp",EDGE,"ef449be0-296d-467a-9b3b-92f5416e835a6.MirrorCS")])]}),makeQuery(id+"FsNRKL0DmnP3UvC_2.opExtrude","SWEPT_FACE",FACE,{"disambiguationData":[OSD([sQuery(id+"F1.wireOp",EDGE,"ef449be0-296d-467a-9b3b-92f5416e835a8.MirrorCS")])]}),makeQuery(id+"FsNRKL0DmnP3UvC_2.opExtrude","SWEPT_FACE",FACE,{"disambiguationData":[OSD([sQuery(id+"F1.wireOp",EDGE,"ef449be0-296d-467a-9b3b-92f5416e835a17.MirrorCS")])]}),makeQuery(id+"FsNRKL0DmnP3UvC_2.opExtrude","SWEPT_FACE",FACE,{"disambiguationData":[OSD([sQuery(id+"F1.wireOp",EDGE,"ef449be0-296d-467a-9b3b-92f5416e835a22.MirrorCS")])]}),makeQuery(id+"FsNRKL0DmnP3UvC_2.opExtrude","SWEPT_FACE",FACE,{"disambiguationData":[OSD([sQuery(id+"F1.wireOp",EDGE,"3edb70b5-b804-4be9-ab85-b3a438d212921.MirrorCS")])]}),makeQuery(id+"FsNRKL0DmnP3UvC_2.opExtrude","SWEPT_FACE",FACE,{"disambiguationData":[OSD([sQuery(id+"F1.wireOp",EDGE,"3edb70b5-b804-4be9-ab85-b3a438d212922.MirrorCS")])]}),makeQuery(id+"FsNRKL0DmnP3UvC_2.opExtrude","SWEPT_FACE",FACE,{"disambiguationData":[OSD([sQuery(id+"F1.wireOp",EDGE,"3edb70b5-b804-4be9-ab85-b3a438d212923.MirrorCS")])]}),makeQuery(id+"FsNRKL0DmnP3UvC_2.opExtrude","SWEPT_FACE",FACE,{"disambiguationData":[OSD([sQuery(id+"F1.wireOp",EDGE,"3edb70b5-b804-4be9-ab85-b3a438d212927.MirrorCS")])]}),makeQuery(id+"FsNRKL0DmnP3UvC_2.opExtrude","SWEPT_FACE",FACE,{"disambiguationData":[OSD([sQuery(id+"F1.wireOp",EDGE,"3edb70b5-b804-4be9-ab85-b3a438d2129211.MirrorCS")])]}),makeQuery(id+"FsNRKL0DmnP3UvC_2.opExtrude","SWEPT_FACE",FACE,{"disambiguationData":[OSD([sQuery(id+"F1.wireOp",EDGE,"3edb70b5-b804-4be9-ab85-b3a438d2129214.MirrorCS")])]}),makeQuery(id+"FsNRKL0DmnP3UvC_2.opExtrude","SWEPT_FACE",FACE,{"disambiguationData":[OSD([sQuery(id+"F1.wireOp",EDGE,"3edb70b5-b804-4be9-ab85-b3a438d2129215.MirrorCS")])]}),makeQuery(id+"FsNRKL0DmnP3UvC_2.opExtrude","SWEPT_FACE",FACE,{"disambiguationData":[OSD([sQuery(id+"F1.wireOp",EDGE,"3edb70b5-b804-4be9-ab85-b3a438d2129216.MirrorCS")])]}),makeQuery(id+"FsNRKL0DmnP3UvC_2.opExtrude","SWEPT_FACE",FACE,{"disambiguationData":[OSD([sQuery(id+"F1.wireOp",EDGE,"3edb70b5-b804-4be9-ab85-b3a438d2129218.MirrorCS")])]}),makeQuery(id+"FsNRKL0DmnP3UvC_2.opExtrude","SWEPT_FACE",FACE,{"disambiguationData":[OSD([sQuery(id+"F1.wireOp",EDGE,"3edb70b5-b804-4be9-ab85-b3a438d2129220.MirrorCS")])]}),makeQuery(id+"FsNRKL0DmnP3UvC_2.opExtrude","SWEPT_FACE",FACE,{"disambiguationData":[OSD([sQuery(id+"F1.wireOp",EDGE,"3edb70b5-b804-4be9-ab85-b3a438d2129225.MirrorCS")])]}),makeQuery(id+"FsNRKL0DmnP3UvC_2.opExtrude","SWEPT_FACE",FACE,{"disambiguationData":[OSD([sQuery(id+"F1.wireOp",EDGE,"3edb70b5-b804-4be9-ab85-b3a438d2129226.MirrorCS")])]}),makeQuery(id+"FsNRKL0DmnP3UvC_2.opExtrude","SWEPT_FACE",FACE,{"disambiguationData":[OSD([sQuery(id+"F1.wireOp",EDGE,"3edb70b5-b804-4be9-ab85-b3a438d2129233.MirrorCS")])]}),makeQuery(id+"FsNRKL0DmnP3UvC_2.opExtrude","SWEPT_FACE",FACE,{"disambiguationData":[OSD([sQuery(id+"F1.wireOp",EDGE,"3edb70b5-b804-4be9-ab85-b3a438d2129246.MirrorCS")])]}),makeQuery(id+"FsNRKL0DmnP3UvC_2.opExtrude","SWEPT_FACE",FACE,{"disambiguationData":[OSD([sQuery(id+"F1.wireOp",EDGE,"3edb70b5-b804-4be9-ab85-b3a438d2129262.MirrorCS")])]}),makeQuery(id+"FsNRKL0DmnP3UvC_2.opExtrude","SWEPT_FACE",FACE,{"disambiguationData":[OSD([sQuery(id+"F1.wireOp",EDGE,"3edb70b5-b804-4be9-ab85-b3a438d2129264.MirrorCS")])]}),makeQuery(id+"FsNRKL0DmnP3UvC_2.opExtrude","SWEPT_FACE",FACE,{"disambiguationData":[OSD([sQuery(id+"F1.wireOp",EDGE,"3edb70b5-b804-4be9-ab85-b3a438d2129271.MirrorCS")])]}),makeQuery(id+"FsNRKL0DmnP3UvC_2.opExtrude","SWEPT_FACE",FACE,{"disambiguationData":[OSD([sQuery(id+"F1.wireOp",EDGE,"3edb70b5-b804-4be9-ab85-b3a438d2129284.MirrorCS")])]}),makeQuery(id+"FsNRKL0DmnP3UvC_2.opExtrude","SWEPT_FACE",FACE,{"disambiguationData":[OSD([sQuery(id+"F1.wireOp",EDGE,"14cc3a12-7d66-4c02-94a9-419769d572550.MirrorCS")])]}),makeQuery(id+"FsNRKL0DmnP3UvC_2.opExtrude","SWEPT_FACE",FACE,{"disambiguationData":[OSD([sQuery(id+"F1.wireOp",EDGE,"14cc3a12-7d66-4c02-94a9-419769d572553.MirrorCS")])]}),makeQuery(id+"FsNRKL0DmnP3UvC_2.opExtrude","SWEPT_FACE",FACE,{"disambiguationData":[OSD([sQuery(id+"F1.wireOp",EDGE,"14cc3a12-7d66-4c02-94a9-419769d572557.MirrorCS")])]}),makeQuery(id+"FsNRKL0DmnP3UvC_2.opExtrude","SWEPT_FACE",FACE,{"disambiguationData":[OSD([sQuery(id+"F1.wireOp",EDGE,"14cc3a12-7d66-4c02-94a9-419769d572558.MirrorCS")])]}),makeQuery(id+"FsNRKL0DmnP3UvC_2.opExtrude","SWEPT_FACE",FACE,{"disambiguationData":[OSD([sQuery(id+"F1.wireOp",EDGE,"14cc3a12-7d66-4c02-94a9-419769d5725512.MirrorCS")])]}),makeQuery(id+"FsNRKL0DmnP3UvC_2.opExtrude","SWEPT_FACE",FACE,{"disambiguationData":[OSD([sQuery(id+"F1.wireOp",EDGE,"14cc3a12-7d66-4c02-94a9-419769d5725514.MirrorCS")])]}),makeQuery(id+"FsNRKL0DmnP3UvC_2.opExtrude","SWEPT_FACE",FACE,{"disambiguationData":[OSD([sQuery(id+"F1.wireOp",EDGE,"14cc3a12-7d66-4c02-94a9-419769d5725515.MirrorCS")])]}),makeQuery(id+"FsNRKL0DmnP3UvC_2.opExtrude","SWEPT_FACE",FACE,{"disambiguationData":[OSD([sQuery(id+"F1.wireOp",EDGE,"14cc3a12-7d66-4c02-94a9-419769d5725517.MirrorCS")])]}),makeQuery(id+"FsNRKL0DmnP3UvC_2.opExtrude","SWEPT_FACE",FACE,{"disambiguationData":[OSD([sQuery(id+"F1.wireOp",EDGE,"14cc3a12-7d66-4c02-94a9-419769d5725522.MirrorCS")])]}),makeQuery(id+"FsNRKL0DmnP3UvC_2.opExtrude","SWEPT_FACE",FACE,{"disambiguationData":[OSD([sQuery(id+"F1.wireOp",EDGE,"14cc3a12-7d66-4c02-94a9-419769d5725531.MirrorCS")])]}),makeQuery(id+"FsNRKL0DmnP3UvC_2.opExtrude","SWEPT_FACE",FACE,{"disambiguationData":[OSD([sQuery(id+"F1.wireOp",EDGE,"14cc3a12-7d66-4c02-94a9-419769d5725540.MirrorCS")])]}),makeQuery(id+"FsNRKL0DmnP3UvC_2.opExtrude","SWEPT_FACE",FACE,{"disambiguationData":[OSD([sQuery(id+"F1.wireOp",EDGE,"14cc3a12-7d66-4c02-94a9-419769d5725550.MirrorCS")])]}),makeQuery(id+"FsNRKL0DmnP3UvC_2.opExtrude","SWEPT_FACE",FACE,{"disambiguationData":[OSD([sQuery(id+"F1.wireOp",EDGE,"E50.top")])]}),makeQuery(id+"FsNRKL0DmnP3UvC_2.opExtrude","SWEPT_FACE",FACE,{"disambiguationData":[OSD([sQuery(id+"F1.wireOp",EDGE,"2bd68e58-e41e-494a-8911-974b16a43e85.top")])]}),makeQuery(id+"FsNRKL0DmnP3UvC_2.opExtrude","SWEPT_FACE",FACE,{"disambiguationData":[OSD([sQuery(id+"F1.wireOp",EDGE,"d6889f29-3aff-4a43-887b-f05846102f70.top")])]}),makeQuery(id+"FsNRKL0DmnP3UvC_2.opExtrude","SWEPT_FACE",FACE,{"disambiguationData":[OSD([sQuery(id+"F1.wireOp",EDGE,"767c3735-2e18-495c-a88c-5e601239b8bc.top")])]}),makeQuery(id+"FsNRKL0DmnP3UvC_2.opExtrude","SWEPT_FACE",FACE,{"disambiguationData":[OSD([sQuery(id+"F1.wireOp",EDGE,"edaeaa6a-4a46-43e7-a4a8-70bf9d0c2d230.MirrorCS")])]}),makeQuery(id+"FsNRKL0DmnP3UvC_2.opExtrude","SWEPT_FACE",FACE,{"disambiguationData":[OSD([sQuery(id+"F1.wireOp",EDGE,"6148efe5-7769-4a6e-beb2-6f02e7a2884e0.MirrorCS")])]}),makeQuery(id+"FsNRKL0DmnP3UvC_2.opExtrude","SWEPT_FACE",FACE,{"disambiguationData":[OSD([sQuery(id+"F1.wireOp",EDGE,"498a5576-9314-4d20-a76d-96ff3a6abcc60.MirrorCS")])]}),makeQuery(id+"FsNRKL0DmnP3UvC_2.opExtrude","SWEPT_FACE",FACE,{"disambiguationData":[OSD([sQuery(id+"F1.wireOp",EDGE,"E52.MirrorCS")])]}),makeQuery(id+"FsNRKL0DmnP3UvC_2.opExtrude","SWEPT_FACE",FACE,{"disambiguationData":[OSD([sQuery(id+"F1.wireOp",EDGE,"E49.top")])]})]});
            var sketch = newSketch(context, id + "F7", { "sketchPlane" : qUnion([Q0])});
            skLineSegment(sketch, "E238.bottom", {"start": v(0, -23) * mm, "end": v(3, -23) * mm});
            skLineSegment(sketch, "E238.top", {"start": v(0, -9) * mm, "end": v(3, -9) * mm});
            skLineSegment(sketch, "E238.left", {"start": v(0, -9) * mm, "end": v(0, -23) * mm});
            skLineSegment(sketch, "E238.right", {"start": v(3, -9) * mm, "end": v(3, -23) * mm});
            skLineSegment(sketch, "E239.bottom", {"start": v(42.6, -23) * mm, "end": v(45.6, -23) * mm});
            skLineSegment(sketch, "E239.top", {"start": v(42.6, -9) * mm, "end": v(45.6, -9) * mm});
            skLineSegment(sketch, "E239.left", {"start": v(42.6, -9) * mm, "end": v(42.6, -23) * mm});
            skLineSegment(sketch, "E239.right", {"start": v(45.6, -9) * mm, "end": v(45.6, -23) * mm});
            skLineSegment(sketch, "E240.bottom", {"start": v(87.05, -23) * mm, "end": v(90.05, -23) * mm});
            skLineSegment(sketch, "E240.top", {"start": v(87.05, -9) * mm, "end": v(90.05, -9) * mm});
            skLineSegment(sketch, "E240.left", {"start": v(87.05, -9) * mm, "end": v(87.05, -23) * mm});
            skLineSegment(sketch, "E240.right", {"start": v(90.05, -9) * mm, "end": v(90.05, -23) * mm});
            skLineSegment(sketch, "E241.bottom", {"start": v(131.5, -23) * mm, "end": v(134.5, -23) * mm});
            skLineSegment(sketch, "E241.top", {"start": v(131.5, -9) * mm, "end": v(134.5, -9) * mm});
            skLineSegment(sketch, "E241.left", {"start": v(131.5, -9) * mm, "end": v(131.5, -23) * mm});
            skLineSegment(sketch, "E241.right", {"start": v(134.5, -9) * mm, "end": v(134.5, -23) * mm});
            skLineSegment(sketch, "E242.bottom", {"start": v(175.95, -23) * mm, "end": v(178.95, -23) * mm});
            skLineSegment(sketch, "E242.top", {"start": v(175.95, -9) * mm, "end": v(178.95, -9) * mm});
            skLineSegment(sketch, "E242.left", {"start": v(175.95, -9) * mm, "end": v(175.95, -23) * mm});
            skLineSegment(sketch, "E242.right", {"start": v(178.95, -9) * mm, "end": v(178.95, -23) * mm});
            skLineSegment(sketch, "E243", {"start": v(177.45, -23) * mm, "end": v(177.45, 0) * mm, "construction": true});
            skPoint(sketch, "E244", {"position": v(44.1, -9) * mm});
            skPoint(sketch, "E245", {"position": v(88.55, -9) * mm});
            skPoint(sketch, "E246", {"position": v(133, -9) * mm});
            skLineSegment(sketch, "E247.MirrorCS", {"start": v(223.4, -9) * mm, "end": v(220.4, -9) * mm});
            skLineSegment(sketch, "E248.MirrorCS", {"start": v(312.3, -9) * mm, "end": v(309.3, -9) * mm});
            skLineSegment(sketch, "E249.MirrorCS", {"start": v(267.85, -9) * mm, "end": v(264.85, -9) * mm});
            skLineSegment(sketch, "E250.MirrorCS", {"start": v(223.4, -9) * mm, "end": v(223.4, -23) * mm});
            skLineSegment(sketch, "E251.MirrorCS", {"start": v(351.9, -9) * mm, "end": v(351.9, -23) * mm});
            skLineSegment(sketch, "E252.MirrorCS", {"start": v(354.9, -9) * mm, "end": v(351.9, -9) * mm});
            skLineSegment(sketch, "E253.MirrorCS", {"start": v(354.9, -9) * mm, "end": v(354.9, -23) * mm});
            skLineSegment(sketch, "E254.MirrorCS", {"start": v(354.9, -23) * mm, "end": v(351.9, -23) * mm});
            skLineSegment(sketch, "E255.MirrorCS", {"start": v(223.4, -23) * mm, "end": v(220.4, -23) * mm});
            skLineSegment(sketch, "E256.MirrorCS", {"start": v(312.3, -23) * mm, "end": v(309.3, -23) * mm});
            skLineSegment(sketch, "E257.MirrorCS", {"start": v(264.85, -9) * mm, "end": v(264.85, -23) * mm});
            skLineSegment(sketch, "E258.MirrorCS", {"start": v(220.4, -9) * mm, "end": v(220.4, -23) * mm});
            skLineSegment(sketch, "E259.MirrorCS", {"start": v(312.3, -9) * mm, "end": v(312.3, -23) * mm});
            skLineSegment(sketch, "E260.MirrorCS", {"start": v(309.3, -9) * mm, "end": v(309.3, -23) * mm});
            skLineSegment(sketch, "E261.MirrorCS", {"start": v(267.85, -9) * mm, "end": v(267.85, -23) * mm});
            skLineSegment(sketch, "E262.MirrorCS", {"start": v(267.85, -23) * mm, "end": v(264.85, -23) * mm});
            skPoint(sketch, "E263.MirrorP", {"position": v(266.35, -9) * mm});
            skPoint(sketch, "E264.MirrorP", {"position": v(310.8, -9) * mm});
            skPoint(sketch, "E265.MirrorP", {"position": v(221.9, -9) * mm});
            skLineSegment(sketch, "E266", {"start": v(0, -17) * mm, "end": v(3, -17) * mm});
            skLineSegment(sketch, "E267.trimOffspring", {"start": v(42.6, -17) * mm, "end": v(45.6, -17) * mm});
            skLineSegment(sketch, "E268.trimOffspring", {"start": v(87.05, -17) * mm, "end": v(90.05, -17) * mm});
            skLineSegment(sketch, "E269.trimOffspring", {"start": v(131.5, -17) * mm, "end": v(134.5, -17) * mm});
            skLineSegment(sketch, "E270.trimOffspring", {"start": v(175.95, -17) * mm, "end": v(178.95, -17) * mm});
            skLineSegment(sketch, "E271.trimOffspring", {"start": v(264.85, -17) * mm, "end": v(267.85, -17) * mm});
            skLineSegment(sketch, "E272.trimOffspring", {"start": v(309.3, -17) * mm, "end": v(312.3, -17) * mm});
            skLineSegment(sketch, "E273.trimOffspring", {"start": v(351.9, -17) * mm, "end": v(354.9, -17) * mm});
            skLineSegment(sketch, "E274.trimOffspring", {"start": v(220.4, -17) * mm, "end": v(223.4, -17) * mm});
            skSolve(sketch);
        }
        {
            var Q0;
            {var subQ0=sQuery(id+"F7.wireOp",EDGE,"E252.MirrorCS");Q0=makeQuery(id+"F7.imprint","IMPRINT",FACE,{"disambiguationData":[TD([[makeQuery(id+"F7.imprint","IMPRINT",EDGE,{"derivedFrom":subQ0}),1.0]])]});}
            var Q1;
            {var subQ0=sQuery(id+"F7.wireOp",EDGE,"E247.MirrorCS");Q1=makeQuery(id+"F7.imprint","IMPRINT",FACE,{"disambiguationData":[TD([[makeQuery(id+"F7.imprint","IMPRINT",EDGE,{"derivedFrom":subQ0}),1.0]])]});}
            var Q2;
            {var subQ0=sQuery(id+"F7.wireOp",EDGE,"E249.MirrorCS");Q2=makeQuery(id+"F7.imprint","IMPRINT",FACE,{"disambiguationData":[TD([[makeQuery(id+"F7.imprint","IMPRINT",EDGE,{"derivedFrom":subQ0}),1.0]])]});}
            var Q3;
            {var subQ0=sQuery(id+"F7.wireOp",EDGE,"E248.MirrorCS");Q3=makeQuery(id+"F7.imprint","IMPRINT",FACE,{"disambiguationData":[TD([[makeQuery(id+"F7.imprint","IMPRINT",EDGE,{"derivedFrom":subQ0}),1.0]])]});}
            var Q4;
            {var subQ0=sQuery(id+"F7.wireOp",EDGE,"E242.top");Q4=makeQuery(id+"F7.imprint","IMPRINT",FACE,{"disambiguationData":[TD([[makeQuery(id+"F7.imprint","IMPRINT",EDGE,{"derivedFrom":subQ0}),-1.0]])]});}
            var Q5;
            {var subQ0=sQuery(id+"F7.wireOp",EDGE,"E241.top");Q5=makeQuery(id+"F7.imprint","IMPRINT",FACE,{"disambiguationData":[TD([[makeQuery(id+"F7.imprint","IMPRINT",EDGE,{"derivedFrom":subQ0}),-1.0]])]});}
            var Q6;
            {var subQ0=sQuery(id+"F7.wireOp",EDGE,"E240.top");Q6=makeQuery(id+"F7.imprint","IMPRINT",FACE,{"disambiguationData":[TD([[makeQuery(id+"F7.imprint","IMPRINT",EDGE,{"derivedFrom":subQ0}),-1.0]])]});}
            var Q7;
            {var subQ0=sQuery(id+"F7.wireOp",EDGE,"E239.top");Q7=makeQuery(id+"F7.imprint","IMPRINT",FACE,{"disambiguationData":[TD([[makeQuery(id+"F7.imprint","IMPRINT",EDGE,{"derivedFrom":subQ0}),-1.0]])]});}
            var Q8;
            {var subQ0=sQuery(id+"F7.wireOp",EDGE,"E238.top");Q8=makeQuery(id+"F7.imprint","IMPRINT",FACE,{"disambiguationData":[TD([[makeQuery(id+"F7.imprint","IMPRINT",EDGE,{"derivedFrom":subQ0}),-1.0]])]});}
            extrude(context, id + "F8", {"entities" : qUnion([Q0, Q1, Q2, Q3, Q4, Q5, Q6, Q7, Q8]), "operationType" : NewBodyOperationType.REMOVE, "endBound" : BoundingType.THROUGH_ALL, "oppositeDirection" : true, "offsetDistance" : 25 * mm, "depth" : 25 * mm});
        }
        {
            var Q0;
            Q0=makeQuery(id+"FsNRKL0DmnP3UvC_2.boolean.opBoolean","MERGE",FACE,{"derivedFrom":[makeQuery(id+"F5.opExtrude","SWEPT_FACE",FACE,{"disambiguationData":[OSD([sQuery(id+"F2.wireOp",EDGE,"E237.top")])]}),makeQuery(id+"FsNRKL0DmnP3UvC_2.opExtrude","SWEPT_FACE",FACE,{"disambiguationData":[OSD([sQuery(id+"F1.wireOp",EDGE,"6a9f6b4e-8c17-479e-95aa-c868ed02bcc8.top")])]}),makeQuery(id+"FsNRKL0DmnP3UvC_2.opExtrude","SWEPT_FACE",FACE,{"disambiguationData":[OSD([sQuery(id+"F1.wireOp",EDGE,"d0e4a734-2a00-432a-b971-5d8aa04fd6d9.top")])]}),makeQuery(id+"FsNRKL0DmnP3UvC_2.opExtrude","SWEPT_FACE",FACE,{"disambiguationData":[OSD([sQuery(id+"F1.wireOp",EDGE,"0fa12c67-d307-4137-8aa7-c6dfb889ed58.top")])]}),makeQuery(id+"FsNRKL0DmnP3UvC_2.opExtrude","SWEPT_FACE",FACE,{"disambiguationData":[OSD([sQuery(id+"F1.wireOp",EDGE,"b24369ca-d6b9-488d-87b8-04e79b56e681.top")])]}),makeQuery(id+"FsNRKL0DmnP3UvC_2.opExtrude","SWEPT_FACE",FACE,{"disambiguationData":[OSD([sQuery(id+"F1.wireOp",EDGE,"bdd40437-d99c-4cb8-ad16-0bfbec51b95a.top")])]}),makeQuery(id+"FsNRKL0DmnP3UvC_2.opExtrude","SWEPT_FACE",FACE,{"disambiguationData":[OSD([sQuery(id+"F1.wireOp",EDGE,"855304bd-eab8-4061-b494-b8053609a213.top")])]}),makeQuery(id+"FsNRKL0DmnP3UvC_2.opExtrude","SWEPT_FACE",FACE,{"disambiguationData":[OSD([sQuery(id+"F1.wireOp",EDGE,"8a604169-f9db-4d10-b6de-17cdce77b9ee7.MirrorCS")])]}),makeQuery(id+"FsNRKL0DmnP3UvC_2.opExtrude","SWEPT_FACE",FACE,{"disambiguationData":[OSD([sQuery(id+"F1.wireOp",EDGE,"8a604169-f9db-4d10-b6de-17cdce77b9ee17.MirrorCS")])]}),makeQuery(id+"FsNRKL0DmnP3UvC_2.opExtrude","SWEPT_FACE",FACE,{"disambiguationData":[OSD([sQuery(id+"F1.wireOp",EDGE,"8a604169-f9db-4d10-b6de-17cdce77b9ee18.MirrorCS")])]}),makeQuery(id+"FsNRKL0DmnP3UvC_2.opExtrude","SWEPT_FACE",FACE,{"disambiguationData":[OSD([sQuery(id+"F1.wireOp",EDGE,"8a604169-f9db-4d10-b6de-17cdce77b9ee20.MirrorCS")])]}),makeQuery(id+"FsNRKL0DmnP3UvC_2.opExtrude","SWEPT_FACE",FACE,{"disambiguationData":[OSD([sQuery(id+"F1.wireOp",EDGE,"8a604169-f9db-4d10-b6de-17cdce77b9ee22.MirrorCS")])]}),makeQuery(id+"FsNRKL0DmnP3UvC_2.opExtrude","SWEPT_FACE",FACE,{"disambiguationData":[OSD([sQuery(id+"F1.wireOp",EDGE,"8a604169-f9db-4d10-b6de-17cdce77b9ee26.MirrorCS")])]}),makeQuery(id+"FsNRKL0DmnP3UvC_2.opExtrude","SWEPT_FACE",FACE,{"disambiguationData":[OSD([sQuery(id+"F1.wireOp",EDGE,"ef449be0-296d-467a-9b3b-92f5416e835a1.MirrorCS")])]}),makeQuery(id+"FsNRKL0DmnP3UvC_2.opExtrude","SWEPT_FACE",FACE,{"disambiguationData":[OSD([sQuery(id+"F1.wireOp",EDGE,"ef449be0-296d-467a-9b3b-92f5416e835a5.MirrorCS")])]}),makeQuery(id+"FsNRKL0DmnP3UvC_2.opExtrude","SWEPT_FACE",FACE,{"disambiguationData":[OSD([sQuery(id+"F1.wireOp",EDGE,"ef449be0-296d-467a-9b3b-92f5416e835a6.MirrorCS")])]}),makeQuery(id+"FsNRKL0DmnP3UvC_2.opExtrude","SWEPT_FACE",FACE,{"disambiguationData":[OSD([sQuery(id+"F1.wireOp",EDGE,"ef449be0-296d-467a-9b3b-92f5416e835a8.MirrorCS")])]}),makeQuery(id+"FsNRKL0DmnP3UvC_2.opExtrude","SWEPT_FACE",FACE,{"disambiguationData":[OSD([sQuery(id+"F1.wireOp",EDGE,"ef449be0-296d-467a-9b3b-92f5416e835a17.MirrorCS")])]}),makeQuery(id+"FsNRKL0DmnP3UvC_2.opExtrude","SWEPT_FACE",FACE,{"disambiguationData":[OSD([sQuery(id+"F1.wireOp",EDGE,"ef449be0-296d-467a-9b3b-92f5416e835a22.MirrorCS")])]}),makeQuery(id+"FsNRKL0DmnP3UvC_2.opExtrude","SWEPT_FACE",FACE,{"disambiguationData":[OSD([sQuery(id+"F1.wireOp",EDGE,"3edb70b5-b804-4be9-ab85-b3a438d212921.MirrorCS")])]}),makeQuery(id+"FsNRKL0DmnP3UvC_2.opExtrude","SWEPT_FACE",FACE,{"disambiguationData":[OSD([sQuery(id+"F1.wireOp",EDGE,"3edb70b5-b804-4be9-ab85-b3a438d212922.MirrorCS")])]}),makeQuery(id+"FsNRKL0DmnP3UvC_2.opExtrude","SWEPT_FACE",FACE,{"disambiguationData":[OSD([sQuery(id+"F1.wireOp",EDGE,"3edb70b5-b804-4be9-ab85-b3a438d212923.MirrorCS")])]}),makeQuery(id+"FsNRKL0DmnP3UvC_2.opExtrude","SWEPT_FACE",FACE,{"disambiguationData":[OSD([sQuery(id+"F1.wireOp",EDGE,"3edb70b5-b804-4be9-ab85-b3a438d212927.MirrorCS")])]}),makeQuery(id+"FsNRKL0DmnP3UvC_2.opExtrude","SWEPT_FACE",FACE,{"disambiguationData":[OSD([sQuery(id+"F1.wireOp",EDGE,"3edb70b5-b804-4be9-ab85-b3a438d2129211.MirrorCS")])]}),makeQuery(id+"FsNRKL0DmnP3UvC_2.opExtrude","SWEPT_FACE",FACE,{"disambiguationData":[OSD([sQuery(id+"F1.wireOp",EDGE,"3edb70b5-b804-4be9-ab85-b3a438d2129214.MirrorCS")])]}),makeQuery(id+"FsNRKL0DmnP3UvC_2.opExtrude","SWEPT_FACE",FACE,{"disambiguationData":[OSD([sQuery(id+"F1.wireOp",EDGE,"3edb70b5-b804-4be9-ab85-b3a438d2129215.MirrorCS")])]}),makeQuery(id+"FsNRKL0DmnP3UvC_2.opExtrude","SWEPT_FACE",FACE,{"disambiguationData":[OSD([sQuery(id+"F1.wireOp",EDGE,"3edb70b5-b804-4be9-ab85-b3a438d2129216.MirrorCS")])]}),makeQuery(id+"FsNRKL0DmnP3UvC_2.opExtrude","SWEPT_FACE",FACE,{"disambiguationData":[OSD([sQuery(id+"F1.wireOp",EDGE,"3edb70b5-b804-4be9-ab85-b3a438d2129218.MirrorCS")])]}),makeQuery(id+"FsNRKL0DmnP3UvC_2.opExtrude","SWEPT_FACE",FACE,{"disambiguationData":[OSD([sQuery(id+"F1.wireOp",EDGE,"3edb70b5-b804-4be9-ab85-b3a438d2129220.MirrorCS")])]}),makeQuery(id+"FsNRKL0DmnP3UvC_2.opExtrude","SWEPT_FACE",FACE,{"disambiguationData":[OSD([sQuery(id+"F1.wireOp",EDGE,"3edb70b5-b804-4be9-ab85-b3a438d2129225.MirrorCS")])]}),makeQuery(id+"FsNRKL0DmnP3UvC_2.opExtrude","SWEPT_FACE",FACE,{"disambiguationData":[OSD([sQuery(id+"F1.wireOp",EDGE,"3edb70b5-b804-4be9-ab85-b3a438d2129226.MirrorCS")])]}),makeQuery(id+"FsNRKL0DmnP3UvC_2.opExtrude","SWEPT_FACE",FACE,{"disambiguationData":[OSD([sQuery(id+"F1.wireOp",EDGE,"3edb70b5-b804-4be9-ab85-b3a438d2129233.MirrorCS")])]}),makeQuery(id+"FsNRKL0DmnP3UvC_2.opExtrude","SWEPT_FACE",FACE,{"disambiguationData":[OSD([sQuery(id+"F1.wireOp",EDGE,"3edb70b5-b804-4be9-ab85-b3a438d2129246.MirrorCS")])]}),makeQuery(id+"FsNRKL0DmnP3UvC_2.opExtrude","SWEPT_FACE",FACE,{"disambiguationData":[OSD([sQuery(id+"F1.wireOp",EDGE,"3edb70b5-b804-4be9-ab85-b3a438d2129262.MirrorCS")])]}),makeQuery(id+"FsNRKL0DmnP3UvC_2.opExtrude","SWEPT_FACE",FACE,{"disambiguationData":[OSD([sQuery(id+"F1.wireOp",EDGE,"3edb70b5-b804-4be9-ab85-b3a438d2129264.MirrorCS")])]}),makeQuery(id+"FsNRKL0DmnP3UvC_2.opExtrude","SWEPT_FACE",FACE,{"disambiguationData":[OSD([sQuery(id+"F1.wireOp",EDGE,"3edb70b5-b804-4be9-ab85-b3a438d2129271.MirrorCS")])]}),makeQuery(id+"FsNRKL0DmnP3UvC_2.opExtrude","SWEPT_FACE",FACE,{"disambiguationData":[OSD([sQuery(id+"F1.wireOp",EDGE,"3edb70b5-b804-4be9-ab85-b3a438d2129284.MirrorCS")])]}),makeQuery(id+"FsNRKL0DmnP3UvC_2.opExtrude","SWEPT_FACE",FACE,{"disambiguationData":[OSD([sQuery(id+"F1.wireOp",EDGE,"14cc3a12-7d66-4c02-94a9-419769d572550.MirrorCS")])]}),makeQuery(id+"FsNRKL0DmnP3UvC_2.opExtrude","SWEPT_FACE",FACE,{"disambiguationData":[OSD([sQuery(id+"F1.wireOp",EDGE,"14cc3a12-7d66-4c02-94a9-419769d572553.MirrorCS")])]}),makeQuery(id+"FsNRKL0DmnP3UvC_2.opExtrude","SWEPT_FACE",FACE,{"disambiguationData":[OSD([sQuery(id+"F1.wireOp",EDGE,"14cc3a12-7d66-4c02-94a9-419769d572557.MirrorCS")])]}),makeQuery(id+"FsNRKL0DmnP3UvC_2.opExtrude","SWEPT_FACE",FACE,{"disambiguationData":[OSD([sQuery(id+"F1.wireOp",EDGE,"14cc3a12-7d66-4c02-94a9-419769d572558.MirrorCS")])]}),makeQuery(id+"FsNRKL0DmnP3UvC_2.opExtrude","SWEPT_FACE",FACE,{"disambiguationData":[OSD([sQuery(id+"F1.wireOp",EDGE,"14cc3a12-7d66-4c02-94a9-419769d5725512.MirrorCS")])]}),makeQuery(id+"FsNRKL0DmnP3UvC_2.opExtrude","SWEPT_FACE",FACE,{"disambiguationData":[OSD([sQuery(id+"F1.wireOp",EDGE,"14cc3a12-7d66-4c02-94a9-419769d5725514.MirrorCS")])]}),makeQuery(id+"FsNRKL0DmnP3UvC_2.opExtrude","SWEPT_FACE",FACE,{"disambiguationData":[OSD([sQuery(id+"F1.wireOp",EDGE,"14cc3a12-7d66-4c02-94a9-419769d5725515.MirrorCS")])]}),makeQuery(id+"FsNRKL0DmnP3UvC_2.opExtrude","SWEPT_FACE",FACE,{"disambiguationData":[OSD([sQuery(id+"F1.wireOp",EDGE,"14cc3a12-7d66-4c02-94a9-419769d5725517.MirrorCS")])]}),makeQuery(id+"FsNRKL0DmnP3UvC_2.opExtrude","SWEPT_FACE",FACE,{"disambiguationData":[OSD([sQuery(id+"F1.wireOp",EDGE,"14cc3a12-7d66-4c02-94a9-419769d5725522.MirrorCS")])]}),makeQuery(id+"FsNRKL0DmnP3UvC_2.opExtrude","SWEPT_FACE",FACE,{"disambiguationData":[OSD([sQuery(id+"F1.wireOp",EDGE,"14cc3a12-7d66-4c02-94a9-419769d5725531.MirrorCS")])]}),makeQuery(id+"FsNRKL0DmnP3UvC_2.opExtrude","SWEPT_FACE",FACE,{"disambiguationData":[OSD([sQuery(id+"F1.wireOp",EDGE,"14cc3a12-7d66-4c02-94a9-419769d5725540.MirrorCS")])]}),makeQuery(id+"FsNRKL0DmnP3UvC_2.opExtrude","SWEPT_FACE",FACE,{"disambiguationData":[OSD([sQuery(id+"F1.wireOp",EDGE,"14cc3a12-7d66-4c02-94a9-419769d5725550.MirrorCS")])]}),makeQuery(id+"FsNRKL0DmnP3UvC_2.opExtrude","SWEPT_FACE",FACE,{"disambiguationData":[OSD([sQuery(id+"F1.wireOp",EDGE,"E50.top")])]}),makeQuery(id+"FsNRKL0DmnP3UvC_2.opExtrude","SWEPT_FACE",FACE,{"disambiguationData":[OSD([sQuery(id+"F1.wireOp",EDGE,"2bd68e58-e41e-494a-8911-974b16a43e85.top")])]}),makeQuery(id+"FsNRKL0DmnP3UvC_2.opExtrude","SWEPT_FACE",FACE,{"disambiguationData":[OSD([sQuery(id+"F1.wireOp",EDGE,"d6889f29-3aff-4a43-887b-f05846102f70.top")])]}),makeQuery(id+"FsNRKL0DmnP3UvC_2.opExtrude","SWEPT_FACE",FACE,{"disambiguationData":[OSD([sQuery(id+"F1.wireOp",EDGE,"767c3735-2e18-495c-a88c-5e601239b8bc.top")])]}),makeQuery(id+"FsNRKL0DmnP3UvC_2.opExtrude","SWEPT_FACE",FACE,{"disambiguationData":[OSD([sQuery(id+"F1.wireOp",EDGE,"edaeaa6a-4a46-43e7-a4a8-70bf9d0c2d230.MirrorCS")])]}),makeQuery(id+"FsNRKL0DmnP3UvC_2.opExtrude","SWEPT_FACE",FACE,{"disambiguationData":[OSD([sQuery(id+"F1.wireOp",EDGE,"6148efe5-7769-4a6e-beb2-6f02e7a2884e0.MirrorCS")])]}),makeQuery(id+"FsNRKL0DmnP3UvC_2.opExtrude","SWEPT_FACE",FACE,{"disambiguationData":[OSD([sQuery(id+"F1.wireOp",EDGE,"498a5576-9314-4d20-a76d-96ff3a6abcc60.MirrorCS")])]}),makeQuery(id+"FsNRKL0DmnP3UvC_2.opExtrude","SWEPT_FACE",FACE,{"disambiguationData":[OSD([sQuery(id+"F1.wireOp",EDGE,"E52.MirrorCS")])]}),makeQuery(id+"FsNRKL0DmnP3UvC_2.opExtrude","SWEPT_FACE",FACE,{"disambiguationData":[OSD([sQuery(id+"F1.wireOp",EDGE,"E49.top")])]})]});
            var sketch = newSketch(context, id + "F9", { "sketchPlane" : qUnion([Q0])});
            skLineSegment(sketch, "E275", {"start": v(3, -17) * mm, "end": v(42.6, -17) * mm, "construction": true});
            skLineSegment(sketch, "E276", {"start": v(45.6, -17) * mm, "end": v(87.05, -17) * mm, "construction": true});
            skLineSegment(sketch, "E277", {"start": v(90.05, -17) * mm, "end": v(131.5, -17) * mm, "construction": true});
            skLineSegment(sketch, "E278", {"start": v(134.5, -17) * mm, "end": v(175.95, -17) * mm});
            skLineSegment(sketch, "E279", {"start": v(178.95, -17) * mm, "end": v(220.4, -17) * mm, "construction": true});
            skLineSegment(sketch, "E280", {"start": v(223.4, -17) * mm, "end": v(264.85, -17) * mm, "construction": true});
            skLineSegment(sketch, "E281", {"start": v(267.85, -17) * mm, "end": v(309.3, -17) * mm, "construction": true});
            skLineSegment(sketch, "E282", {"start": v(312.3, -17) * mm, "end": v(351.9, -17) * mm, "construction": true});
            skCircle(sketch, "E283", {"center": v(288.58, -9) * mm, "radius": 2 * mm});
            skPoint(sketch, "E283.centerSnap0", {"position": v(288.58, -17) * mm});
            skCircle(sketch, "E284", {"center": v(244.13, -17) * mm, "radius": 2 * mm});
            skCircle(sketch, "E285", {"center": v(199.68, -9) * mm, "radius": 2 * mm});
            skPoint(sketch, "E285.centerSnap0", {"position": v(199.68, -17) * mm});
            skCircle(sketch, "E286", {"center": v(155.23, -17) * mm, "radius": 2 * mm});
            skCircle(sketch, "E287", {"center": v(110.78, -9) * mm, "radius": 2 * mm});
            skPoint(sketch, "E287.centerSnap0", {"position": v(110.78, -17) * mm});
            skCircle(sketch, "E288", {"center": v(22.8, -9) * mm, "radius": 2 * mm});
            skPoint(sketch, "E288.centerSnap0", {"position": v(22.8, -8.74) * mm});
            skCircle(sketch, "E289", {"center": v(66.33, -17) * mm, "radius": 2 * mm});
            skCircle(sketch, "E290", {"center": v(332.1, -17) * mm, "radius": 2 * mm});
            skLineSegment(sketch, "E291", {"start": v(22.8, -9) * mm, "end": v(22.8, -17) * mm, "construction": true});
            skSolve(sketch);
        }
        {
            var Q0;
            Q0=makeQuery(id+"F9.imprint","IMPRINT",FACE,{"disambiguationData":[TD([[makeQuery(id+"F9.imprint","IMPRINT",EDGE,{"derivedFrom":sQuery(id+"F9.wireOp",EDGE,"E290")}),1.0]])]});
            var Q1;
            Q1=makeQuery(id+"F9.imprint","IMPRINT",FACE,{"disambiguationData":[TD([[makeQuery(id+"F9.imprint","IMPRINT",EDGE,{"derivedFrom":sQuery(id+"F9.wireOp",EDGE,"E283")}),1.0]])]});
            var Q2;
            Q2=makeQuery(id+"F9.imprint","IMPRINT",FACE,{"disambiguationData":[TD([[makeQuery(id+"F9.imprint","IMPRINT",EDGE,{"derivedFrom":sQuery(id+"F9.wireOp",EDGE,"E284")}),1.0]])]});
            var Q3;
            {var subQ0=sQuery(id+"F9.wireOp",EDGE,"E286");var subQ1=sQuery(id+"F9.wireOp",EDGE,"E278");var subQ3=makeQuery(id+"F9.imprint","INTERSECT",VERTEX,{"disambiguationData":[OD(0.0)],"derivedFrom":[subQ1,subQ0]});Q3=makeQuery(id+"F9.imprint","IMPRINT",FACE,{"disambiguationData":[TD([[makeQuery(id+"F9.imprint","IMPRINT",EDGE,{"disambiguationData":[TD([[subQ3,-1.0]])],"derivedFrom":subQ1}),1.0]])]});}
            var Q4;
            {var subQ0=sQuery(id+"F9.wireOp",EDGE,"E286");var subQ1=sQuery(id+"F9.wireOp",EDGE,"E278");var subQ3=makeQuery(id+"F9.imprint","INTERSECT",VERTEX,{"disambiguationData":[OD(0.0)],"derivedFrom":[subQ1,subQ0]});Q4=makeQuery(id+"F9.imprint","IMPRINT",FACE,{"disambiguationData":[TD([[makeQuery(id+"F9.imprint","IMPRINT",EDGE,{"disambiguationData":[TD([[subQ3,-1.0]])],"derivedFrom":subQ1}),-1.0]])]});}
            var Q5;
            Q5=makeQuery(id+"F9.imprint","IMPRINT",FACE,{"disambiguationData":[TD([[makeQuery(id+"F9.imprint","IMPRINT",EDGE,{"derivedFrom":sQuery(id+"F9.wireOp",EDGE,"E285")}),1.0]])]});
            var Q6;
            Q6=makeQuery(id+"F9.imprint","IMPRINT",FACE,{"disambiguationData":[TD([[makeQuery(id+"F9.imprint","IMPRINT",EDGE,{"derivedFrom":sQuery(id+"F9.wireOp",EDGE,"E289")}),1.0]])]});
            var Q7;
            Q7=makeQuery(id+"F9.imprint","IMPRINT",FACE,{"disambiguationData":[TD([[makeQuery(id+"F9.imprint","IMPRINT",EDGE,{"derivedFrom":sQuery(id+"F9.wireOp",EDGE,"E287")}),1.0]])]});
            var Q8;
            Q8=makeQuery(id+"F9.imprint","IMPRINT",FACE,{"disambiguationData":[TD([[makeQuery(id+"F9.imprint","IMPRINT",EDGE,{"derivedFrom":sQuery(id+"F9.wireOp",EDGE,"E288")}),1.0]])]});
            extrude(context, id + "F10", {"entities" : qUnion([Q0, Q1, Q2, Q3, Q4, Q5, Q6, Q7, Q8]), "operationType" : NewBodyOperationType.REMOVE, "endBound" : BoundingType.THROUGH_ALL, "oppositeDirection" : true, "depth" : 25 * mm});
        }
        {
            var Q0;
            Q0=makeQuery(id+"F3.opExtrude","CAP_FACE",FACE,{"disambiguationData":[OSD([sQuery(id+"F0.wireOp",EDGE,"E0.bottom"),sQuery(id+"F0.wireOp",EDGE,"E0.top"),sQuery(id+"F0.wireOp",EDGE,"E0.left"),sQuery(id+"F0.wireOp",EDGE,"E0.right"),sQuery(id+"F0.wireOp",EDGE,"E1"),sQuery(id+"F0.wireOp",EDGE,"E2"),sQuery(id+"F0.wireOp",EDGE,"E3"),sQuery(id+"F0.wireOp",EDGE,"E4"),sQuery(id+"F0.wireOp",EDGE,"E5"),sQuery(id+"F0.wireOp",EDGE,"E6"),sQuery(id+"F0.wireOp",EDGE,"E7"),sQuery(id+"F0.wireOp",EDGE,"E8"),sQuery(id+"F0.wireOp",EDGE,"E9"),sQuery(id+"F0.wireOp",EDGE,"E10"),sQuery(id+"F0.wireOp",EDGE,"E11"),sQuery(id+"F0.wireOp",EDGE,"E12"),sQuery(id+"F0.wireOp",EDGE,"E13"),sQuery(id+"F0.wireOp",EDGE,"E14"),sQuery(id+"F0.wireOp",EDGE,"E15"),sQuery(id+"F0.wireOp",EDGE,"E16")])],"isStart":false});
            var sketch = newSketch(context, id + "F11", { "sketchPlane" : qUnion([Q0])});
            skLineSegment(sketch, "E292.bottom", {"start": v(0, 12) * mm, "end": v(3, 12) * mm});
            skLineSegment(sketch, "E292.top", {"start": v(0, 9) * mm, "end": v(3, 9) * mm});
            skLineSegment(sketch, "E292.left", {"start": v(0, 12) * mm, "end": v(0, 9) * mm});
            skLineSegment(sketch, "E292.right", {"start": v(3, 12) * mm, "end": v(3, 9) * mm});
            skLineSegment(sketch, "E293.bottom", {"start": v(42.6, 12) * mm, "end": v(45.6, 12) * mm});
            skLineSegment(sketch, "E293.top", {"start": v(42.6, 9) * mm, "end": v(45.6, 9) * mm});
            skLineSegment(sketch, "E293.left", {"start": v(42.6, 12) * mm, "end": v(42.6, 9) * mm});
            skLineSegment(sketch, "E293.right", {"start": v(45.6, 12) * mm, "end": v(45.6, 9) * mm});
            skLineSegment(sketch, "E294.bottom", {"start": v(90.05, 12) * mm, "end": v(87.05, 12) * mm});
            skLineSegment(sketch, "E294.top", {"start": v(90.05, 9) * mm, "end": v(87.05, 9) * mm});
            skLineSegment(sketch, "E294.left", {"start": v(90.05, 12) * mm, "end": v(90.05, 9) * mm});
            skLineSegment(sketch, "E294.right", {"start": v(87.05, 12) * mm, "end": v(87.05, 9) * mm});
            skLineSegment(sketch, "E295.bottom", {"start": v(134.5, 12) * mm, "end": v(131.5, 12) * mm});
            skLineSegment(sketch, "E295.top", {"start": v(134.5, 9) * mm, "end": v(131.5, 9) * mm});
            skLineSegment(sketch, "E295.left", {"start": v(134.5, 12) * mm, "end": v(134.5, 9) * mm});
            skLineSegment(sketch, "E295.right", {"start": v(131.5, 12) * mm, "end": v(131.5, 9) * mm});
            skLineSegment(sketch, "E296.bottom", {"start": v(178.95, 12) * mm, "end": v(175.95, 12) * mm});
            skLineSegment(sketch, "E296.top", {"start": v(178.95, 9) * mm, "end": v(175.95, 9) * mm});
            skLineSegment(sketch, "E296.left", {"start": v(178.95, 12) * mm, "end": v(178.95, 9) * mm});
            skLineSegment(sketch, "E296.right", {"start": v(175.95, 12) * mm, "end": v(175.95, 9) * mm});
            skLineSegment(sketch, "E297.bottom", {"start": v(223.4, 12) * mm, "end": v(220.4, 12) * mm});
            skLineSegment(sketch, "E297.top", {"start": v(223.4, 9) * mm, "end": v(220.4, 9) * mm});
            skLineSegment(sketch, "E297.left", {"start": v(223.4, 12) * mm, "end": v(223.4, 9) * mm});
            skLineSegment(sketch, "E297.right", {"start": v(220.4, 12) * mm, "end": v(220.4, 9) * mm});
            skLineSegment(sketch, "E298.bottom", {"start": v(267.85, 12) * mm, "end": v(264.85, 12) * mm});
            skLineSegment(sketch, "E298.top", {"start": v(267.85, 9) * mm, "end": v(264.85, 9) * mm});
            skLineSegment(sketch, "E298.left", {"start": v(267.85, 12) * mm, "end": v(267.85, 9) * mm});
            skLineSegment(sketch, "E298.right", {"start": v(264.85, 12) * mm, "end": v(264.85, 9) * mm});
            skLineSegment(sketch, "E299.bottom", {"start": v(309.3, 12) * mm, "end": v(312.3, 12) * mm});
            skLineSegment(sketch, "E299.top", {"start": v(309.3, 9) * mm, "end": v(312.3, 9) * mm});
            skLineSegment(sketch, "E299.left", {"start": v(309.3, 12) * mm, "end": v(309.3, 9) * mm});
            skLineSegment(sketch, "E299.right", {"start": v(312.3, 12) * mm, "end": v(312.3, 9) * mm});
            skLineSegment(sketch, "E300.bottom", {"start": v(354.9, 12) * mm, "end": v(351.9, 12) * mm});
            skLineSegment(sketch, "E300.top", {"start": v(354.9, 9) * mm, "end": v(351.9, 9) * mm});
            skLineSegment(sketch, "E300.left", {"start": v(354.9, 12) * mm, "end": v(354.9, 9) * mm});
            skLineSegment(sketch, "E300.right", {"start": v(351.9, 12) * mm, "end": v(351.9, 9) * mm});
            skSolve(sketch);
        }
        {
            var Q0;
            Q0=makeQuery(id+"F11.imprint","IMPRINT",FACE,{"disambiguationData":[TD([[makeQuery(id+"F11.imprint","IMPRINT",EDGE,{"derivedFrom":sQuery(id+"F11.wireOp",EDGE,"E292.bottom")}),-1.0]])]});
            var Q1;
            Q1=makeQuery(id+"F11.imprint","IMPRINT",FACE,{"disambiguationData":[TD([[makeQuery(id+"F11.imprint","IMPRINT",EDGE,{"derivedFrom":sQuery(id+"F11.wireOp",EDGE,"E293.bottom")}),-1.0]])]});
            var Q2;
            Q2=makeQuery(id+"F11.imprint","IMPRINT",FACE,{"disambiguationData":[TD([[makeQuery(id+"F11.imprint","IMPRINT",EDGE,{"derivedFrom":sQuery(id+"F11.wireOp",EDGE,"E294.bottom")}),-1.0]])]});
            var Q3;
            Q3=makeQuery(id+"F11.imprint","IMPRINT",FACE,{"disambiguationData":[TD([[makeQuery(id+"F11.imprint","IMPRINT",EDGE,{"derivedFrom":sQuery(id+"F11.wireOp",EDGE,"E295.bottom")}),-1.0]])]});
            var Q4;
            Q4=makeQuery(id+"F11.imprint","IMPRINT",FACE,{"disambiguationData":[TD([[makeQuery(id+"F11.imprint","IMPRINT",EDGE,{"derivedFrom":sQuery(id+"F11.wireOp",EDGE,"E296.bottom")}),-1.0]])]});
            var Q5;
            Q5=makeQuery(id+"F11.imprint","IMPRINT",FACE,{"disambiguationData":[TD([[makeQuery(id+"F11.imprint","IMPRINT",EDGE,{"derivedFrom":sQuery(id+"F11.wireOp",EDGE,"E297.bottom")}),-1.0]])]});
            var Q6;
            Q6=makeQuery(id+"F11.imprint","IMPRINT",FACE,{"disambiguationData":[TD([[makeQuery(id+"F11.imprint","IMPRINT",EDGE,{"derivedFrom":sQuery(id+"F11.wireOp",EDGE,"E298.bottom")}),-1.0]])]});
            var Q7;
            Q7=makeQuery(id+"F11.imprint","IMPRINT",FACE,{"disambiguationData":[TD([[makeQuery(id+"F11.imprint","IMPRINT",EDGE,{"derivedFrom":sQuery(id+"F11.wireOp",EDGE,"E299.bottom")}),-1.0]])]});
            var Q8;
            Q8=makeQuery(id+"F11.imprint","IMPRINT",FACE,{"disambiguationData":[TD([[makeQuery(id+"F11.imprint","IMPRINT",EDGE,{"derivedFrom":sQuery(id+"F11.wireOp",EDGE,"E300.bottom")}),-1.0]])]});
            extrude(context, id + "F12", {"entities" : qUnion([Q0, Q1, Q2, Q3, Q4, Q5, Q6, Q7, Q8]), "operationType" : NewBodyOperationType.REMOVE, "endBound" : BoundingType.THROUGH_ALL, "oppositeDirection" : true, "depth" : 25 * mm, "offsetDistance" : 25 * mm});
        }
        {
            var Q0;
            {var subQ0=sQuery(id+"F1.wireOp",EDGE,"E49.left");Q0=makeQuery(id+"F8.boolean.opBoolean","SPLIT",FACE,{"disambiguationData":[TD([makeQuery(id+"F8.opExtrude","SWEPT_FACE",FACE,{"disambiguationData":[OSD([sQuery(id+"F7.wireOp",EDGE,"E238.top")])]})])],"derivedFrom":makeQuery(id+"FsNRKL0DmnP3UvC_2.boolean.opBoolean","MERGE",FACE,{"derivedFrom":[makeQuery(id+"F5.opExtrude","SWEPT_FACE",FACE,{"disambiguationData":[OSD([sQuery(id+"F2.wireOp",EDGE,"E237.left")])]}),makeQuery(id+"FsNRKL0DmnP3UvC_2.opExtrude","SWEPT_FACE",FACE,{"disambiguationData":[OSD([subQ0])]})]})});}
            var sketch = newSketch(context, id + "F13", { "sketchPlane" : qUnion([Q0])});
            skLineSegment(sketch, "E301", {"start": v(23, 3) * mm, "end": v(23, 6) * mm});
            skLineSegment(sketch, "E302", {"start": v(23, 6) * mm, "end": v(6, 12) * mm});
            skLineSegment(sketch, "E303", {"start": v(0, 12) * mm, "end": v(6, 12) * mm});
            skLineSegment(sketch, "E304", {"start": v(3, 9) * mm, "end": v(0, 9) * mm});
            skLineSegment(sketch, "E305", {"start": v(3, 9) * mm, "end": v(3, 3) * mm});
            skLineSegment(sketch, "E306", {"start": v(17, 0) * mm, "end": v(9, 0) * mm});
            skLineSegment(sketch, "E307", {"start": v(17, 0) * mm, "end": v(17, 3) * mm});
            skLineSegment(sketch, "E308", {"start": v(23, 3) * mm, "end": v(17, 3) * mm});
            skPoint(sketch, "E309.orphan", {"position": v(23, 0) * mm});
            skLineSegment(sketch, "E310", {"start": v(0, 9) * mm, "end": v(0, 12) * mm});
            skLineSegment(sketch, "E311", {"start": v(3, 3) * mm, "end": v(9, 3) * mm});
            skLineSegment(sketch, "E312", {"start": v(9, 0) * mm, "end": v(9, 3) * mm});
            skSolve(sketch);
        }
        {
            var Q0;
            Q0=makeQuery(id+"F13.imprint","IMPRINT",FACE,{"disambiguationData":[TD([[makeQuery(id+"F13.imprint","IMPRINT",EDGE,{"derivedFrom":sQuery(id+"F13.wireOp",EDGE,"E301")}),-1.0]])]});
            var Q1;
            Q1=makeQuery(id+"F13.imprint","IMPRINT",FACE,{"disambiguationData":[TD([[makeQuery(id+"F13.imprint","IMPRINT",EDGE,{"derivedFrom":sQuery(id+"F13.wireOp",EDGE,"E301")}),1.0]])]});
            extrude(context, id + "F14", {"entities" : qUnion([Q0, Q1]), "oppositeDirection" : true, "offsetDistance" : 25 * mm, "depth" : 3 * mm});
        }
    });
